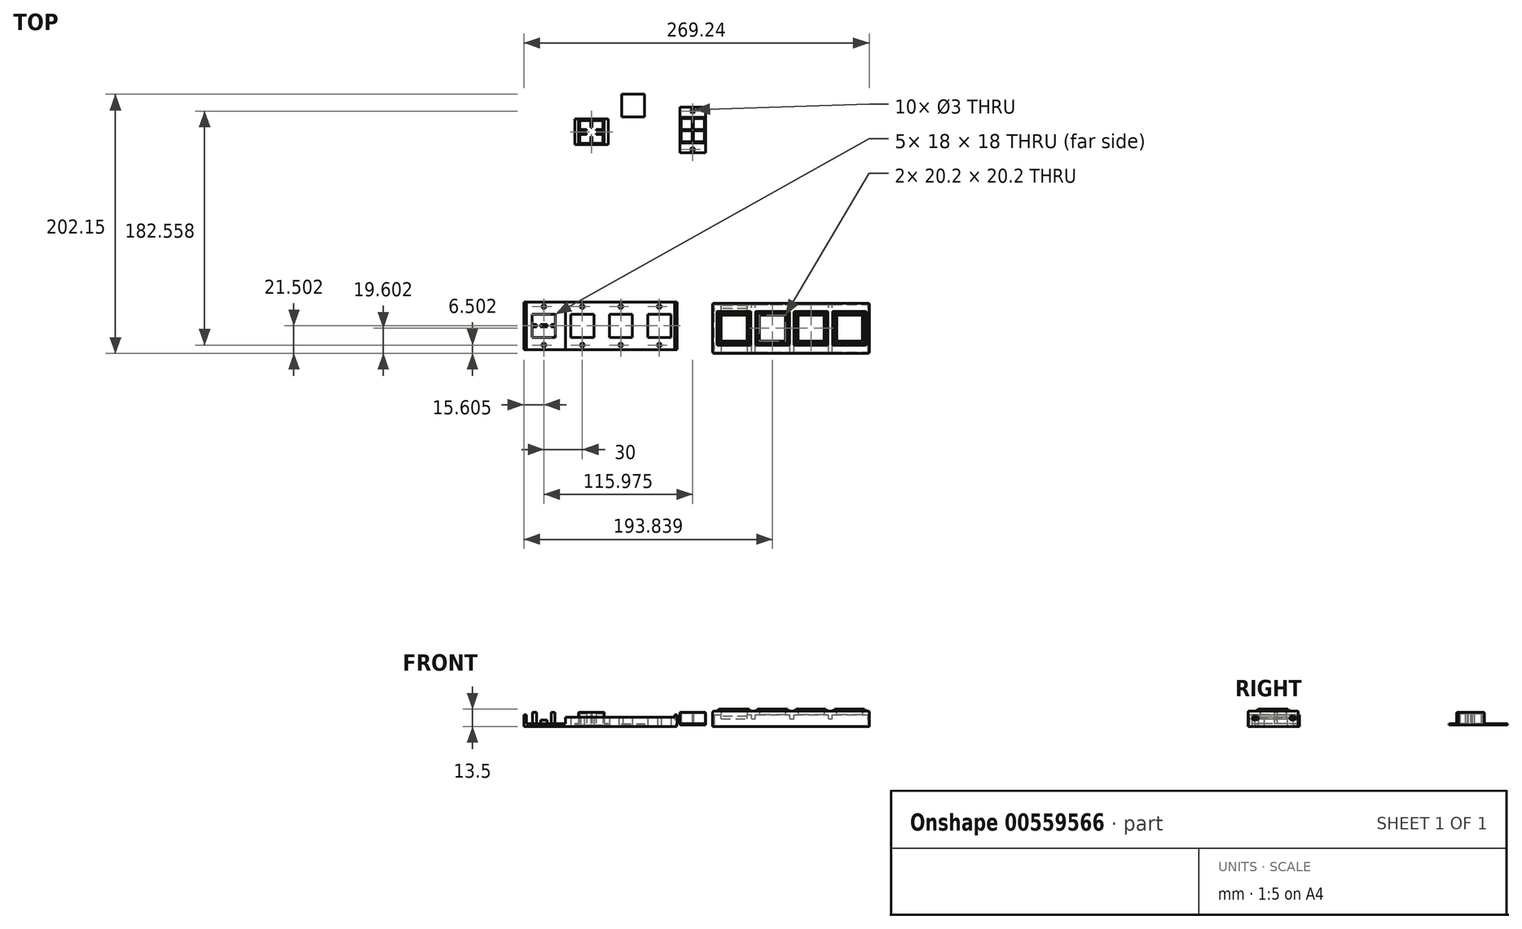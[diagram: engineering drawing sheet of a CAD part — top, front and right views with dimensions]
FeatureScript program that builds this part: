
annotation { "Feature Type Name" : "Feature", "Feature Type Description" : "" }
export const myFeature = defineFeature(function(context is Context, id is Id, definition is map)
    precondition{}
    {
        {
            var Q0;
            Q0=qCreatedBy(makeId("Top.planeOp"),FACE);
            var sketch = newSketch(context, id + "F0", { "sketchPlane" : qUnion([Q0])});
            skPoint(sketch, "E0.middle", {"position": v(0, 0) * mm});
            skLineSegment(sketch, "E1.bottom", {"start": v(10, -10) * mm, "end": v(-10, -10) * mm});
            skLineSegment(sketch, "E1.top", {"start": v(10, 10) * mm, "end": v(-10, 10) * mm});
            skLineSegment(sketch, "E1.left", {"start": v(10, -10) * mm, "end": v(10, 10) * mm});
            skLineSegment(sketch, "E1.right", {"start": v(-10, -10) * mm, "end": v(-10, 10) * mm});
            skSolve(sketch);
        }
        {
            var Q0;
            Q0=makeQuery(id+"F0.imprint","IMPRINT",FACE,{"disambiguationData":[TD([[makeQuery(id+"F0.imprint","IMPRINT",EDGE,{"derivedFrom":sQuery(id+"F0.wireOp",EDGE,"E1.bottom")}),-1.0]])]});
            extrude(context, id + "F1", {"entities" : qUnion([Q0]), "depth" : 10 * mm});
        }
        {
            var Q0;
            Q0=makeQuery(id+"F1.opExtrude","CAP_FACE",FACE,{"disambiguationData":[OSD([sQuery(id+"F0.wireOp",EDGE,"E1.bottom"),sQuery(id+"F0.wireOp",EDGE,"E1.top"),sQuery(id+"F0.wireOp",EDGE,"E1.left"),sQuery(id+"F0.wireOp",EDGE,"E1.right")])],"isStart":true});
            shell(context, id + "F2", {"entities" : qUnion([Q0]), "thickness" : 1 * mm});
        }
        {
            var Q0;
            Q0=qCreatedBy(makeId("Top.planeOp"),FACE);
            var sketch = newSketch(context, id + "F3", { "sketchPlane" : qUnion([Q0])});
            skLineSegment(sketch, "E2.bottom", {"start": v(0.5, -9) * mm, "end": v(-0.5, -9) * mm});
            skLineSegment(sketch, "E2.top", {"start": v(0.5, 9) * mm, "end": v(-0.5, 9) * mm});
            skLineSegment(sketch, "E2.left", {"start": v(0.5, -9) * mm, "end": v(0.5, -0.5) * mm});
            skLineSegment(sketch, "E2.right", {"start": v(-0.5, -9) * mm, "end": v(-0.5, -0.5) * mm});
            skLineSegment(sketch, "E3.bottom", {"start": v(9, 0.5) * mm, "end": v(0.5, 0.5) * mm});
            skLineSegment(sketch, "E3.top", {"start": v(9, -0.5) * mm, "end": v(0.5, -0.5) * mm});
            skLineSegment(sketch, "E3.left", {"start": v(9, 0.5) * mm, "end": v(9, -0.5) * mm});
            skLineSegment(sketch, "E3.right", {"start": v(-9, 0.5) * mm, "end": v(-9, -0.5) * mm});
            skLineSegment(sketch, "E4.trimOffspring", {"start": v(-0.5, 0.5) * mm, "end": v(-0.5, 9) * mm});
            skLineSegment(sketch, "E5.trimOffspring", {"start": v(-0.5, -0.5) * mm, "end": v(-9, -0.5) * mm});
            skLineSegment(sketch, "E6.trimOffspring", {"start": v(0.5, 0.5) * mm, "end": v(0.5, 9) * mm});
            skLineSegment(sketch, "E7.trimOffspring", {"start": v(-0.5, 0.5) * mm, "end": v(-9, 0.5) * mm});
            skSolve(sketch);
        }
        {
            var Q0;
            Q0=qSketchRegion(id+"F3",true);
            extrude(context, id + "F4", {"entities" : qUnion([Q0]), "operationType" : NewBodyOperationType.ADD, "depth" : 9 * mm});
        }
        {
            var Q0;
            Q0=qCreatedBy(makeId("Top.planeOp"),FACE);
            var sketch = newSketch(context, id + "F5", { "sketchPlane" : qUnion([Q0])});
            skLineSegment(sketch, "E8.bottom", {"start": v(-10, -9.5) * mm, "end": v(10, -9.5) * mm});
            skLineSegment(sketch, "E8.top", {"start": v(-10, -17.5) * mm, "end": v(10, -17.5) * mm});
            skLineSegment(sketch, "E8.left", {"start": v(-10, -9.5) * mm, "end": v(-10, -17.5) * mm});
            skLineSegment(sketch, "E8.right", {"start": v(10, -9.5) * mm, "end": v(10, -17.5) * mm});
            skLineSegment(sketch, "E9.bottom", {"start": v(-10, 10) * mm, "end": v(10, 10) * mm});
            skLineSegment(sketch, "E9.top", {"start": v(-10, 18) * mm, "end": v(10, 18) * mm});
            skLineSegment(sketch, "E9.left", {"start": v(-10, 10) * mm, "end": v(-10, 18) * mm});
            skLineSegment(sketch, "E9.right", {"start": v(10, 10) * mm, "end": v(10, 18) * mm});
            skLineSegment(sketch, "E10.bottom", {"start": v(-10, -9.5) * mm, "end": v(-13, -9.5) * mm, "construction": true});
            skLineSegment(sketch, "E10.top", {"start": v(-10, 10) * mm, "end": v(-13, 10) * mm, "construction": true});
            skLineSegment(sketch, "E10.left", {"start": v(-10, -9.5) * mm, "end": v(-10, 10) * mm});
            skLineSegment(sketch, "E10.right", {"start": v(-13, -9.5) * mm, "end": v(-13, 10) * mm, "construction": true});
            skLineSegment(sketch, "E11.bottom", {"start": v(10, -9.5) * mm, "end": v(13, -9.5) * mm, "construction": true});
            skLineSegment(sketch, "E11.top", {"start": v(10, 10) * mm, "end": v(13, 10) * mm, "construction": true});
            skLineSegment(sketch, "E11.left", {"start": v(10, -9.5) * mm, "end": v(10, 10) * mm});
            skLineSegment(sketch, "E11.right", {"start": v(13, -9.5) * mm, "end": v(13, 10) * mm, "construction": true});
            skCircle(sketch, "E12", {"center": v(0, 15) * mm, "radius": 1.5 * mm});
            skCircle(sketch, "E13", {"center": v(0, -15) * mm, "radius": 1.5 * mm});
            skSolve(sketch);
        }
        {
            var Q0;
            Q0=makeQuery(id+"F5.imprint","IMPRINT",FACE,{"disambiguationData":[TD([[makeQuery(id+"F5.imprint","IMPRINT",EDGE,{"derivedFrom":sQuery(id+"F5.wireOp",EDGE,"E10.bottom")}),-1.0]])]});
            var Q1;
            Q1=makeQuery(id+"F5.imprint","IMPRINT",FACE,{"disambiguationData":[TD([[makeQuery(id+"F5.imprint","IMPRINT",EDGE,{"derivedFrom":sQuery(id+"F5.wireOp",EDGE,"E8.bottom")}),-1.0]])]});
            var Q2;
            Q2=makeQuery(id+"F5.imprint","IMPRINT",FACE,{"disambiguationData":[TD([[makeQuery(id+"F5.imprint","IMPRINT",EDGE,{"derivedFrom":sQuery(id+"F5.wireOp",EDGE,"E11.bottom")}),1.0]])]});
            var Q3;
            Q3=makeQuery(id+"F5.imprint","IMPRINT",FACE,{"disambiguationData":[TD([[makeQuery(id+"F5.imprint","IMPRINT",EDGE,{"derivedFrom":sQuery(id+"F5.wireOp",EDGE,"E9.bottom")}),1.0]])]});
            extrude(context, id + "F6", {"entities" : qUnion([Q0, Q1, Q2, Q3]), "operationType" : NewBodyOperationType.ADD, "depth" : 1 * mm});
        }
        {
            var Q0;
            Q0=qCreatedBy(makeId("Top.planeOp"),FACE);
            var sketch = newSketch(context, id + "F7", { "sketchPlane" : qUnion([Q0])});
            skLineSegment(sketch, "E14.bottom", {"start": v(-88.88, 8.7) * mm, "end": v(-68.88, 8.7) * mm});
            skLineSegment(sketch, "E14.top", {"start": v(-88.88, -11.3) * mm, "end": v(-68.88, -11.3) * mm});
            skLineSegment(sketch, "E14.left", {"start": v(-88.88, 8.7) * mm, "end": v(-88.88, -11.3) * mm});
            skLineSegment(sketch, "E14.right", {"start": v(-68.88, 8.7) * mm, "end": v(-68.88, -11.3) * mm});
            skSolve(sketch);
        }
        {
            var Q0;
            Q0=makeQuery(id+"F7.imprint","IMPRINT",FACE,{"disambiguationData":[TD([[makeQuery(id+"F7.imprint","IMPRINT",EDGE,{"derivedFrom":sQuery(id+"F7.wireOp",EDGE,"E14.bottom")}),-1.0]])]});
            extrude(context, id + "F8", {"entities" : qUnion([Q0]), "depth" : 10 * mm});
        }
        {
            var Q0;
            Q0=makeQuery(id+"F13.boolean.opBoolean","MERGE",FACE,{"derivedFrom":[makeQuery(id+"F8.opExtrude","CAP_FACE",FACE,{"disambiguationData":[OSD([sQuery(id+"F7.wireOp",EDGE,"E14.bottom"),sQuery(id+"F7.wireOp",EDGE,"E14.top"),sQuery(id+"F7.wireOp",EDGE,"E14.left"),sQuery(id+"F7.wireOp",EDGE,"E14.right")])],"isStart":true}),makeQuery(id+"F13.opExtrude","CAP_FACE",FACE,{"disambiguationData":[OSD([sQuery(id+"F12.wireOp",EDGE,"E22.bottom"),sQuery(id+"F12.wireOp",EDGE,"E22.top"),sQuery(id+"F12.wireOp",EDGE,"E22.left"),sQuery(id+"F12.wireOp",EDGE,"E22.right"),sQuery(id+"F12.wireOp",EDGE,"E23.trimOffspring"),sQuery(id+"F12.wireOp",EDGE,"E25.trimOffspring"),sQuery(id+"F12.wireOp",EDGE,"E27"),sQuery(id+"F12.wireOp",EDGE,"E28"),sQuery(id+"F12.wireOp",EDGE,"E29.bottom"),sQuery(id+"F12.wireOp",EDGE,"E29.top"),sQuery(id+"F12.wireOp",EDGE,"E29.left"),sQuery(id+"F12.wireOp",EDGE,"E30.bottom"),sQuery(id+"F12.wireOp",EDGE,"E30.top"),sQuery(id+"F12.wireOp",EDGE,"E30.left"),sQuery(id+"F12.wireOp",EDGE,"E31.bottom"),sQuery(id+"F12.wireOp",EDGE,"E31.top"),sQuery(id+"F12.wireOp",EDGE,"E31.right"),sQuery(id+"F12.wireOp",EDGE,"E32.bottom"),sQuery(id+"F12.wireOp",EDGE,"E32.top"),sQuery(id+"F12.wireOp",EDGE,"E32.right")])],"isStart":true})]});
            var sketch = newSketch(context, id + "F9", { "sketchPlane" : qUnion([Q0])});
            skLineSegment(sketch, "E15.bottom", {"start": v(-88.88, 11.3) * mm, "end": v(-68.88, 11.3) * mm});
            skLineSegment(sketch, "E15.top", {"start": v(-88.88, 14.3) * mm, "end": v(-68.88, 14.3) * mm, "construction": true});
            skLineSegment(sketch, "E15.left", {"start": v(-88.88, 11.3) * mm, "end": v(-88.88, 14.3) * mm, "construction": true});
            skLineSegment(sketch, "E15.right", {"start": v(-68.88, 11.3) * mm, "end": v(-68.88, 14.3) * mm, "construction": true});
            skLineSegment(sketch, "E16.bottom", {"start": v(-88.88, -8.7) * mm, "end": v(-68.88, -8.7) * mm});
            skLineSegment(sketch, "E16.top", {"start": v(-88.88, -11.7) * mm, "end": v(-68.88, -11.7) * mm});
            skLineSegment(sketch, "E16.left", {"start": v(-88.88, -8.7) * mm, "end": v(-88.88, -11.7) * mm, "construction": true});
            skLineSegment(sketch, "E16.right", {"start": v(-68.88, -8.7) * mm, "end": v(-68.88, -11.7) * mm, "construction": true});
            skLineSegment(sketch, "E17.bottom", {"start": v(-88.88, -8.7) * mm, "end": v(-91.88, -8.7) * mm});
            skLineSegment(sketch, "E17.top", {"start": v(-88.88, 11.3) * mm, "end": v(-91.88, 11.3) * mm});
            skLineSegment(sketch, "E17.left", {"start": v(-88.88, -8.7) * mm, "end": v(-88.88, 11.3) * mm});
            skLineSegment(sketch, "E17.right", {"start": v(-91.88, -8.7) * mm, "end": v(-91.88, 11.3) * mm});
            skLineSegment(sketch, "E18.bottom", {"start": v(-68.88, -8.7) * mm, "end": v(-65.88, -8.7) * mm});
            skLineSegment(sketch, "E18.top", {"start": v(-68.88, 11.3) * mm, "end": v(-65.88, 11.3) * mm});
            skLineSegment(sketch, "E18.left", {"start": v(-68.88, -8.7) * mm, "end": v(-68.88, 11.3) * mm});
            skLineSegment(sketch, "E18.right", {"start": v(-65.88, -8.7) * mm, "end": v(-65.88, 11.3) * mm});
            skLineSegment(sketch, "E19.bottom", {"start": v(-88.88, -11.7) * mm, "end": v(-68.88, -11.7) * mm, "construction": true});
            skLineSegment(sketch, "E19.top", {"start": v(-88.88, -16.7) * mm, "end": v(-68.88, -16.7) * mm, "construction": true});
            skLineSegment(sketch, "E19.left", {"start": v(-88.88, -11.7) * mm, "end": v(-88.88, -16.7) * mm, "construction": true});
            skLineSegment(sketch, "E19.right", {"start": v(-68.88, -11.7) * mm, "end": v(-68.88, -16.7) * mm, "construction": true});
            skCircle(sketch, "E20", {"center": v(-78.88, -13.7) * mm, "radius": 1.5 * mm, "construction": true});
            skSolve(sketch);
        }
        {
            var Q0;
            Q0=qSketchRegion(id+"F9",true);
            extrude(context, id + "F10", {"entities" : qUnion([Q0]), "operationType" : NewBodyOperationType.ADD, "oppositeDirection" : true, "depth" : 0.95 * mm});
        }
        {
            var Q0;
            Q0=makeQuery(id+"F8.opExtrude","CAP_FACE",FACE,{"disambiguationData":[OSD([sQuery(id+"F7.wireOp",EDGE,"E14.bottom"),sQuery(id+"F7.wireOp",EDGE,"E14.top"),sQuery(id+"F7.wireOp",EDGE,"E14.left"),sQuery(id+"F7.wireOp",EDGE,"E14.right")])],"isStart":true});
            shell(context, id + "F11", {"entities" : qUnion([Q0]), "thickness" : 1 * mm});
        }
        {
            var Q0;
            Q0=qCreatedBy(makeId("Top.planeOp"),FACE);
            var sketch = newSketch(context, id + "F12", { "sketchPlane" : qUnion([Q0])});
            skLineSegment(sketch, "E21.bottom", {"start": v(-87.88, -0.1) * mm, "end": v(-79.38, -0.1) * mm, "construction": true});
            skLineSegment(sketch, "E21.top", {"start": v(-87.88, -2.5) * mm, "end": v(-79.38, -2.5) * mm, "construction": true});
            skLineSegment(sketch, "E21.left", {"start": v(-87.88, -0.1) * mm, "end": v(-87.88, -2.5) * mm, "construction": true});
            skLineSegment(sketch, "E21.right", {"start": v(-69.88, -0.1) * mm, "end": v(-69.88, -2.5) * mm, "construction": true});
            skLineSegment(sketch, "E22.bottom", {"start": v(-79.38, 7.7) * mm, "end": v(-78.38, 7.7) * mm});
            skLineSegment(sketch, "E22.top", {"start": v(-79.38, -10.3) * mm, "end": v(-78.38, -10.3) * mm});
            skLineSegment(sketch, "E22.left", {"start": v(-79.38, 7.7) * mm, "end": v(-79.38, -0.1) * mm});
            skLineSegment(sketch, "E22.right", {"start": v(-78.38, 7.7) * mm, "end": v(-78.38, -0.1) * mm});
            skLineSegment(sketch, "E23.trimOffspring", {"start": v(-79.38, -10.3) * mm, "end": v(-79.38, -2.5) * mm});
            skLineSegment(sketch, "E24.trimOffspring", {"start": v(-78.38, -0.1) * mm, "end": v(-69.88, -0.1) * mm, "construction": true});
            skLineSegment(sketch, "E25.trimOffspring", {"start": v(-78.38, -2.5) * mm, "end": v(-78.38, -10.3) * mm});
            skLineSegment(sketch, "E26.trimOffspring", {"start": v(-78.38, -2.5) * mm, "end": v(-69.88, -2.5) * mm, "construction": true});
            skLineSegment(sketch, "E27", {"start": v(-79.38, -2.5) * mm, "end": v(-79.38, -0.1) * mm});
            skLineSegment(sketch, "E28", {"start": v(-78.38, -2.5) * mm, "end": v(-78.38, -0.1) * mm});
            skLineSegment(sketch, "E29.bottom", {"start": v(-87.88, -2.5) * mm, "end": v(-79.38, -2.5) * mm});
            skLineSegment(sketch, "E29.top", {"start": v(-87.88, -3.3) * mm, "end": v(-79.38, -3.3) * mm});
            skLineSegment(sketch, "E29.left", {"start": v(-87.88, -2.5) * mm, "end": v(-87.88, -3.3) * mm});
            skLineSegment(sketch, "E29.right", {"start": v(-79.38, -2.5) * mm, "end": v(-79.38, -3.3) * mm});
            skLineSegment(sketch, "E30.bottom", {"start": v(-87.88, -0.1) * mm, "end": v(-79.38, -0.1) * mm});
            skLineSegment(sketch, "E30.top", {"start": v(-87.88, 0.7) * mm, "end": v(-79.38, 0.7) * mm});
            skLineSegment(sketch, "E30.left", {"start": v(-87.88, -0.1) * mm, "end": v(-87.88, 0.7) * mm});
            skLineSegment(sketch, "E30.right", {"start": v(-79.38, -0.1) * mm, "end": v(-79.38, 0.7) * mm});
            skLineSegment(sketch, "E31.bottom", {"start": v(-78.38, -3.3) * mm, "end": v(-69.88, -3.3) * mm});
            skLineSegment(sketch, "E31.top", {"start": v(-78.38, -2.5) * mm, "end": v(-69.88, -2.5) * mm});
            skLineSegment(sketch, "E31.left", {"start": v(-78.38, -3.3) * mm, "end": v(-78.38, -2.5) * mm});
            skLineSegment(sketch, "E31.right", {"start": v(-69.88, -3.3) * mm, "end": v(-69.88, -2.5) * mm});
            skLineSegment(sketch, "E32.bottom", {"start": v(-78.38, -0.1) * mm, "end": v(-69.88, -0.1) * mm});
            skLineSegment(sketch, "E32.top", {"start": v(-78.38, 0.7) * mm, "end": v(-69.88, 0.7) * mm});
            skLineSegment(sketch, "E32.left", {"start": v(-78.38, -0.1) * mm, "end": v(-78.38, 0.7) * mm});
            skLineSegment(sketch, "E32.right", {"start": v(-69.88, -0.1) * mm, "end": v(-69.88, 0.7) * mm});
            skSolve(sketch);
        }
        {
            var Q0;
            Q0=makeQuery(id+"F12.imprint","IMPRINT",FACE,{"disambiguationData":[TD([[makeQuery(id+"F12.imprint","IMPRINT",EDGE,{"derivedFrom":sQuery(id+"F12.wireOp",EDGE,"E22.bottom")}),-1.0]])]});
            var Q1;
            Q1=makeQuery(id+"F12.imprint","IMPRINT",FACE,{"disambiguationData":[TD([[makeQuery(id+"F12.imprint","IMPRINT",EDGE,{"derivedFrom":sQuery(id+"F12.wireOp",EDGE,"E29.bottom")}),-1.0]])]});
            var Q2;
            Q2=makeQuery(id+"F12.imprint","IMPRINT",FACE,{"disambiguationData":[TD([[makeQuery(id+"F12.imprint","IMPRINT",EDGE,{"derivedFrom":sQuery(id+"F12.wireOp",EDGE,"E30.bottom")}),1.0]])]});
            var Q3;
            Q3=makeQuery(id+"F12.imprint","IMPRINT",FACE,{"disambiguationData":[TD([[makeQuery(id+"F12.imprint","IMPRINT",EDGE,{"derivedFrom":sQuery(id+"F12.wireOp",EDGE,"E32.bottom")}),1.0]])]});
            var Q4;
            Q4=makeQuery(id+"F12.imprint","IMPRINT",FACE,{"disambiguationData":[TD([[makeQuery(id+"F12.imprint","IMPRINT",EDGE,{"derivedFrom":sQuery(id+"F12.wireOp",EDGE,"E31.bottom")}),1.0]])]});
            var Q5;
            Q5=sQuery(id+"F12.wireOp",EDGE,"E22.left");
            var Q6;
            Q6=sQuery(id+"F12.wireOp",EDGE,"E23.trimOffspring");
            var Q7;
            Q7=sQuery(id+"F12.wireOp",EDGE,"E21.top");
            var Q8;
            Q8=sQuery(id+"F12.wireOp",EDGE,"E24.trimOffspring");
            var Q9;
            Q9=sQuery(id+"F12.wireOp",EDGE,"E22.bottom");
            var Q10;
            Q10=sQuery(id+"F12.wireOp",EDGE,"E22.right");
            var Q11;
            Q11=sQuery(id+"F12.wireOp",EDGE,"E22.top");
            var Q12;
            Q12=sQuery(id+"F12.wireOp",EDGE,"E21.bottom");
            var Q13;
            Q13=sQuery(id+"F12.wireOp",EDGE,"E25.trimOffspring");
            var Q14;
            Q14=sQuery(id+"F12.wireOp",EDGE,"E26.trimOffspring");
            var Q15;
            Q15=sQuery(id+"F12.wireOp",EDGE,"E21.right");
            var Q16;
            Q16=sQuery(id+"F12.wireOp",EDGE,"E21.left");
            extrude(context, id + "F13", {"entities" : qUnion([Q0, Q1, Q2, Q3, Q4]), "operationType" : NewBodyOperationType.ADD, "surfaceEntities" : qUnion([Q5, Q6, Q7, Q8, Q9, Q10, Q11, Q12, Q13, Q14, Q15, Q16]), "depth" : 9 * mm});
        }
        {
            var Q0;
            Q0=makeQuery(id+"F13.boolean.opBoolean","MERGE",FACE,{"derivedFrom":[makeQuery(id+"F8.opExtrude","CAP_FACE",FACE,{"disambiguationData":[OSD([sQuery(id+"F7.wireOp",EDGE,"E14.bottom"),sQuery(id+"F7.wireOp",EDGE,"E14.top"),sQuery(id+"F7.wireOp",EDGE,"E14.left"),sQuery(id+"F7.wireOp",EDGE,"E14.right")])],"isStart":true}),makeQuery(id+"F13.opExtrude","CAP_FACE",FACE,{"disambiguationData":[OSD([sQuery(id+"F12.wireOp",EDGE,"E21.bottom"),sQuery(id+"F12.wireOp",EDGE,"E21.top"),sQuery(id+"F12.wireOp",EDGE,"E21.left"),sQuery(id+"F12.wireOp",EDGE,"E21.right"),sQuery(id+"F12.wireOp",EDGE,"E22.bottom"),sQuery(id+"F12.wireOp",EDGE,"E22.top"),sQuery(id+"F12.wireOp",EDGE,"E22.left"),sQuery(id+"F12.wireOp",EDGE,"E22.right"),sQuery(id+"F12.wireOp",EDGE,"E23.trimOffspring"),sQuery(id+"F12.wireOp",EDGE,"E24.trimOffspring"),sQuery(id+"F12.wireOp",EDGE,"E25.trimOffspring"),sQuery(id+"F12.wireOp",EDGE,"E26.trimOffspring")])],"isStart":true})]});
            var sketch = newSketch(context, id + "F14", { "sketchPlane" : qUnion([Q0])});
            skLineSegment(sketch, "E33.bottom", {"start": v(-75.28, -2.3) * mm, "end": v(-82.48, -2.3) * mm});
            skLineSegment(sketch, "E33.top", {"start": v(-75.28, 4.9) * mm, "end": v(-82.48, 4.9) * mm});
            skLineSegment(sketch, "E33.left", {"start": v(-75.28, -2.3) * mm, "end": v(-75.28, 4.9) * mm});
            skLineSegment(sketch, "E33.right", {"start": v(-82.48, -2.3) * mm, "end": v(-82.48, 4.9) * mm});
            skPoint(sketch, "E33.middle.positionSnap1", {"position": v(-88.88, 1.8) * mm});
            skSolve(sketch);
        }
        {
            var Q0;
            {var subQ1=makeQuery(id+"F13.opExtrude","CAP_EDGE",EDGE,{"disambiguationData":[OSD([sQuery(id+"F12.wireOp",EDGE,"E22.right")])],"isStart":true});var subQ3=sQuery(id+"F14.wireOp",EDGE,"E33.bottom");var subQ4=makeQuery(id+"F14.imprint","INTERSECT",VERTEX,{"derivedFrom":[subQ1,subQ3]});Q0=makeQuery(id+"F14.imprint","IMPRINT",FACE,{"disambiguationData":[TD([[makeQuery(id+"F14.imprint","IMPRINT",EDGE,{"disambiguationData":[TD([[subQ4,-1.0]])],"derivedFrom":subQ3}),-1.0]])]});}
            extrude(context, id + "F15", {"entities" : qUnion([Q0]), "operationType" : NewBodyOperationType.REMOVE, "oppositeDirection" : true, "depth" : 9 * mm});
        }
        {
            var Q0;
            Q0=qCreatedBy(makeId("Top.planeOp"),FACE);
            var sketch = newSketch(context, id + "F16", { "sketchPlane" : qUnion([Q0])});
            skLineSegment(sketch, "E34.bottom", {"start": v(-124.98, -143.56) * mm, "end": v(-106.98, -143.56) * mm});
            skLineSegment(sketch, "E34.top", {"start": v(-124.98, -161.56) * mm, "end": v(-106.98, -161.56) * mm});
            skLineSegment(sketch, "E34.left", {"start": v(-124.98, -143.56) * mm, "end": v(-124.98, -161.56) * mm});
            skLineSegment(sketch, "E34.right", {"start": v(-106.98, -143.56) * mm, "end": v(-106.98, -161.56) * mm});
            skLineSegment(sketch, "E35.bottom", {"start": v(-116.73, -143.56) * mm, "end": v(-115.23, -143.56) * mm, "construction": true});
            skLineSegment(sketch, "E35.top", {"start": v(-116.73, -161.56) * mm, "end": v(-115.23, -161.56) * mm, "construction": true});
            skLineSegment(sketch, "E35.left", {"start": v(-116.73, -143.56) * mm, "end": v(-116.73, -151.56) * mm, "construction": true});
            skLineSegment(sketch, "E35.right", {"start": v(-115.23, -143.56) * mm, "end": v(-115.23, -151.56) * mm, "construction": true});
            skCircle(sketch, "E36", {"center": v(-115.98, -137.56) * mm, "radius": 1.5 * mm});
            skPoint(sketch, "E37", {"position": v(-115.98, -143.56) * mm});
            skCircle(sketch, "E38", {"center": v(-115.98, -167.56) * mm, "radius": 1.5 * mm});
            skLineSegment(sketch, "E39.trimOffspring", {"start": v(-115.23, -151.56) * mm, "end": v(-112.23, -151.56) * mm, "construction": true});
            skLineSegment(sketch, "E40.trimOffspring", {"start": v(-115.23, -153.56) * mm, "end": v(-112.23, -153.56) * mm, "construction": true});
            skLineSegment(sketch, "E41.trimOffspring", {"start": v(-116.73, -153.56) * mm, "end": v(-116.73, -161.56) * mm, "construction": true});
            skLineSegment(sketch, "E42.trimOffspring", {"start": v(-115.23, -153.56) * mm, "end": v(-115.23, -161.56) * mm, "construction": true});
            skLineSegment(sketch, "E43.bottom", {"start": v(-121.73, -143.56) * mm, "end": v(-119.73, -143.56) * mm});
            skLineSegment(sketch, "E43.top", {"start": v(-121.73, -161.56) * mm, "end": v(-119.73, -161.56) * mm});
            skLineSegment(sketch, "E43.left", {"start": v(-121.73, -143.56) * mm, "end": v(-121.73, -151.56) * mm});
            skLineSegment(sketch, "E43.right", {"start": v(-119.73, -143.56) * mm, "end": v(-119.73, -151.56) * mm});
            skLineSegment(sketch, "E44.bottom", {"start": v(-112.23, -143.56) * mm, "end": v(-110.23, -143.56) * mm});
            skLineSegment(sketch, "E44.top", {"start": v(-112.23, -161.56) * mm, "end": v(-110.23, -161.56) * mm});
            skLineSegment(sketch, "E44.left", {"start": v(-112.23, -143.56) * mm, "end": v(-112.23, -151.56) * mm});
            skLineSegment(sketch, "E44.right", {"start": v(-110.23, -143.56) * mm, "end": v(-110.23, -151.56) * mm});
            skLineSegment(sketch, "E45.bottom", {"start": v(-124.98, -151.56) * mm, "end": v(-121.73, -151.56) * mm});
            skLineSegment(sketch, "E45.top", {"start": v(-124.98, -153.56) * mm, "end": v(-121.73, -153.56) * mm});
            skLineSegment(sketch, "E45.left", {"start": v(-124.98, -151.56) * mm, "end": v(-124.98, -153.56) * mm});
            skLineSegment(sketch, "E45.right", {"start": v(-106.98, -151.56) * mm, "end": v(-106.98, -153.56) * mm});
            skLineSegment(sketch, "E46.trimOffspring", {"start": v(-121.73, -153.56) * mm, "end": v(-121.73, -161.56) * mm});
            skLineSegment(sketch, "E47.trimOffspring", {"start": v(-119.73, -153.56) * mm, "end": v(-119.73, -161.56) * mm});
            skLineSegment(sketch, "E48.trimOffspring", {"start": v(-119.73, -151.56) * mm, "end": v(-116.73, -151.56) * mm, "construction": true});
            skLineSegment(sketch, "E49.trimOffspring", {"start": v(-119.73, -153.56) * mm, "end": v(-116.73, -153.56) * mm, "construction": true});
            skLineSegment(sketch, "E50.trimOffspring", {"start": v(-119.73, -151.56) * mm, "end": v(-112.23, -151.56) * mm});
            skLineSegment(sketch, "E51.trimOffspring", {"start": v(-119.73, -153.56) * mm, "end": v(-112.23, -153.56) * mm});
            skLineSegment(sketch, "E52.trimOffspring", {"start": v(-112.23, -153.56) * mm, "end": v(-112.23, -161.56) * mm});
            skLineSegment(sketch, "E53.trimOffspring", {"start": v(-110.23, -153.56) * mm, "end": v(-110.23, -161.56) * mm});
            skLineSegment(sketch, "E54.trimOffspring", {"start": v(-110.23, -151.56) * mm, "end": v(-106.98, -151.56) * mm});
            skLineSegment(sketch, "E55.trimOffspring", {"start": v(-110.23, -153.56) * mm, "end": v(-106.98, -153.56) * mm});
            skLineSegment(sketch, "E56.bottom", {"start": v(-94.98, -143.56) * mm, "end": v(-76.98, -143.56) * mm});
            skLineSegment(sketch, "E56.top", {"start": v(-94.98, -161.56) * mm, "end": v(-76.98, -161.56) * mm});
            skLineSegment(sketch, "E56.left", {"start": v(-94.98, -143.56) * mm, "end": v(-94.98, -161.56) * mm});
            skLineSegment(sketch, "E56.right", {"start": v(-76.98, -143.56) * mm, "end": v(-76.98, -161.56) * mm});
            skLineSegment(sketch, "E57.bottom", {"start": v(-86.73, -143.56) * mm, "end": v(-85.23, -143.56) * mm, "construction": true});
            skLineSegment(sketch, "E57.top", {"start": v(-86.73, -161.56) * mm, "end": v(-85.23, -161.56) * mm, "construction": true});
            skLineSegment(sketch, "E57.left", {"start": v(-86.73, -143.56) * mm, "end": v(-86.73, -151.56) * mm, "construction": true});
            skLineSegment(sketch, "E57.right", {"start": v(-85.23, -143.56) * mm, "end": v(-85.23, -151.56) * mm, "construction": true});
            skLineSegment(sketch, "E58.bottom", {"start": v(-94.98, -151.56) * mm, "end": v(-91.73, -151.56) * mm, "construction": true});
            skLineSegment(sketch, "E58.top", {"start": v(-94.98, -153.56) * mm, "end": v(-91.73, -153.56) * mm, "construction": true});
            skLineSegment(sketch, "E58.left", {"start": v(-94.98, -151.56) * mm, "end": v(-94.98, -153.56) * mm, "construction": true});
            skLineSegment(sketch, "E58.right", {"start": v(-76.98, -151.56) * mm, "end": v(-76.98, -153.56) * mm, "construction": true});
            skCircle(sketch, "E59", {"center": v(-85.98, -137.56) * mm, "radius": 1.5 * mm});
            skPoint(sketch, "E60", {"position": v(-85.98, -143.56) * mm});
            skCircle(sketch, "E61", {"center": v(-85.98, -167.56) * mm, "radius": 1.5 * mm});
            skLineSegment(sketch, "E62.trimOffspring", {"start": v(-85.23, -151.56) * mm, "end": v(-82.23, -151.56) * mm, "construction": true});
            skLineSegment(sketch, "E63.trimOffspring", {"start": v(-85.23, -153.56) * mm, "end": v(-82.23, -153.56) * mm, "construction": true});
            skLineSegment(sketch, "E64.trimOffspring", {"start": v(-86.73, -153.56) * mm, "end": v(-86.73, -161.56) * mm, "construction": true});
            skLineSegment(sketch, "E65.trimOffspring", {"start": v(-85.23, -153.56) * mm, "end": v(-85.23, -161.56) * mm, "construction": true});
            skLineSegment(sketch, "E66.bottom", {"start": v(-91.73, -143.56) * mm, "end": v(-89.73, -143.56) * mm});
            skLineSegment(sketch, "E66.top", {"start": v(-91.73, -161.56) * mm, "end": v(-89.73, -161.56) * mm});
            skLineSegment(sketch, "E66.left", {"start": v(-91.73, -143.56) * mm, "end": v(-91.73, -151.56) * mm});
            skLineSegment(sketch, "E66.right", {"start": v(-89.73, -143.56) * mm, "end": v(-89.73, -151.56) * mm});
            skLineSegment(sketch, "E67.bottom", {"start": v(-82.23, -143.56) * mm, "end": v(-80.23, -143.56) * mm});
            skLineSegment(sketch, "E67.top", {"start": v(-82.23, -161.56) * mm, "end": v(-80.23, -161.56) * mm});
            skLineSegment(sketch, "E67.left", {"start": v(-82.23, -143.56) * mm, "end": v(-82.23, -151.56) * mm});
            skLineSegment(sketch, "E67.right", {"start": v(-80.23, -143.56) * mm, "end": v(-80.23, -151.56) * mm});
            skLineSegment(sketch, "E68.bottom", {"start": v(-94.98, -151.56) * mm, "end": v(-91.73, -151.56) * mm});
            skLineSegment(sketch, "E68.top", {"start": v(-94.98, -153.56) * mm, "end": v(-91.73, -153.56) * mm});
            skLineSegment(sketch, "E68.left", {"start": v(-94.98, -151.56) * mm, "end": v(-94.98, -153.56) * mm});
            skLineSegment(sketch, "E68.right", {"start": v(-76.98, -151.56) * mm, "end": v(-76.98, -153.56) * mm});
            skLineSegment(sketch, "E69.trimOffspring", {"start": v(-91.73, -153.56) * mm, "end": v(-91.73, -161.56) * mm});
            skLineSegment(sketch, "E70.trimOffspring", {"start": v(-89.73, -153.56) * mm, "end": v(-89.73, -161.56) * mm});
            skLineSegment(sketch, "E71.trimOffspring", {"start": v(-89.73, -151.56) * mm, "end": v(-86.73, -151.56) * mm, "construction": true});
            skLineSegment(sketch, "E72.trimOffspring", {"start": v(-89.73, -153.56) * mm, "end": v(-86.73, -153.56) * mm, "construction": true});
            skLineSegment(sketch, "E73.trimOffspring", {"start": v(-89.73, -151.56) * mm, "end": v(-82.23, -151.56) * mm});
            skLineSegment(sketch, "E74.trimOffspring", {"start": v(-89.73, -153.56) * mm, "end": v(-82.23, -153.56) * mm});
            skLineSegment(sketch, "E75.trimOffspring", {"start": v(-82.23, -153.56) * mm, "end": v(-82.23, -161.56) * mm});
            skLineSegment(sketch, "E76.trimOffspring", {"start": v(-80.23, -151.56) * mm, "end": v(-76.98, -151.56) * mm, "construction": true});
            skLineSegment(sketch, "E77.trimOffspring", {"start": v(-80.23, -153.56) * mm, "end": v(-80.23, -161.56) * mm});
            skLineSegment(sketch, "E78.trimOffspring", {"start": v(-80.23, -151.56) * mm, "end": v(-76.98, -151.56) * mm});
            skLineSegment(sketch, "E79.trimOffspring", {"start": v(-80.23, -153.56) * mm, "end": v(-76.98, -153.56) * mm, "construction": true});
            skLineSegment(sketch, "E80.trimOffspring", {"start": v(-80.23, -153.56) * mm, "end": v(-76.98, -153.56) * mm});
            skLineSegment(sketch, "E81.bottom", {"start": v(-64.98, -143.56) * mm, "end": v(-46.98, -143.56) * mm});
            skLineSegment(sketch, "E81.top", {"start": v(-64.98, -161.56) * mm, "end": v(-46.98, -161.56) * mm});
            skLineSegment(sketch, "E81.left", {"start": v(-64.98, -143.56) * mm, "end": v(-64.98, -161.56) * mm});
            skLineSegment(sketch, "E81.right", {"start": v(-46.98, -143.56) * mm, "end": v(-46.98, -161.56) * mm});
            skLineSegment(sketch, "E82.bottom", {"start": v(-64.98, -161.56) * mm, "end": v(-47.98, -161.56) * mm});
            skLineSegment(sketch, "E83.bottom", {"start": v(-56.73, -143.56) * mm, "end": v(-55.23, -143.56) * mm, "construction": true});
            skLineSegment(sketch, "E83.top", {"start": v(-56.73, -161.56) * mm, "end": v(-55.23, -161.56) * mm, "construction": true});
            skLineSegment(sketch, "E83.left", {"start": v(-56.73, -143.56) * mm, "end": v(-56.73, -151.56) * mm, "construction": true});
            skLineSegment(sketch, "E83.right", {"start": v(-55.23, -143.56) * mm, "end": v(-55.23, -151.56) * mm, "construction": true});
            skLineSegment(sketch, "E84.bottom", {"start": v(-64.98, -151.56) * mm, "end": v(-61.73, -151.56) * mm, "construction": true});
            skLineSegment(sketch, "E84.top", {"start": v(-64.98, -153.56) * mm, "end": v(-61.73, -153.56) * mm, "construction": true});
            skLineSegment(sketch, "E84.left", {"start": v(-64.98, -151.56) * mm, "end": v(-64.98, -153.56) * mm, "construction": true});
            skLineSegment(sketch, "E84.right", {"start": v(-46.98, -151.56) * mm, "end": v(-46.98, -153.56) * mm, "construction": true});
            skCircle(sketch, "E85", {"center": v(-55.98, -137.56) * mm, "radius": 1.5 * mm});
            skPoint(sketch, "E86", {"position": v(-55.98, -143.56) * mm});
            skCircle(sketch, "E87", {"center": v(-55.98, -167.56) * mm, "radius": 1.5 * mm});
            skLineSegment(sketch, "E88.trimOffspring", {"start": v(-55.23, -151.56) * mm, "end": v(-52.23, -151.56) * mm, "construction": true});
            skLineSegment(sketch, "E89.trimOffspring", {"start": v(-55.23, -153.56) * mm, "end": v(-52.23, -153.56) * mm, "construction": true});
            skLineSegment(sketch, "E90.trimOffspring", {"start": v(-56.73, -153.56) * mm, "end": v(-56.73, -161.56) * mm, "construction": true});
            skLineSegment(sketch, "E91.trimOffspring", {"start": v(-55.23, -153.56) * mm, "end": v(-55.23, -161.56) * mm, "construction": true});
            skLineSegment(sketch, "E92.bottom", {"start": v(-61.73, -143.56) * mm, "end": v(-59.73, -143.56) * mm});
            skLineSegment(sketch, "E92.top", {"start": v(-61.73, -161.56) * mm, "end": v(-59.73, -161.56) * mm});
            skLineSegment(sketch, "E92.left", {"start": v(-61.73, -143.56) * mm, "end": v(-61.73, -151.56) * mm});
            skLineSegment(sketch, "E92.right", {"start": v(-59.73, -143.56) * mm, "end": v(-59.73, -151.56) * mm});
            skLineSegment(sketch, "E93.bottom", {"start": v(-52.23, -143.56) * mm, "end": v(-50.23, -143.56) * mm});
            skLineSegment(sketch, "E93.top", {"start": v(-52.23, -161.56) * mm, "end": v(-50.23, -161.56) * mm});
            skLineSegment(sketch, "E93.left", {"start": v(-52.23, -143.56) * mm, "end": v(-52.23, -151.56) * mm});
            skLineSegment(sketch, "E93.right", {"start": v(-50.23, -143.56) * mm, "end": v(-50.23, -151.56) * mm});
            skLineSegment(sketch, "E94.bottom", {"start": v(-64.98, -151.56) * mm, "end": v(-61.73, -151.56) * mm});
            skLineSegment(sketch, "E94.top", {"start": v(-64.98, -153.56) * mm, "end": v(-61.73, -153.56) * mm});
            skLineSegment(sketch, "E94.left", {"start": v(-64.98, -151.56) * mm, "end": v(-64.98, -153.56) * mm});
            skLineSegment(sketch, "E94.right", {"start": v(-46.98, -151.56) * mm, "end": v(-46.98, -153.56) * mm});
            skLineSegment(sketch, "E95.trimOffspring", {"start": v(-61.73, -153.56) * mm, "end": v(-61.73, -161.56) * mm});
            skLineSegment(sketch, "E96.trimOffspring", {"start": v(-59.73, -153.56) * mm, "end": v(-59.73, -161.56) * mm});
            skLineSegment(sketch, "E97.trimOffspring", {"start": v(-59.73, -151.56) * mm, "end": v(-56.73, -151.56) * mm, "construction": true});
            skLineSegment(sketch, "E98.trimOffspring", {"start": v(-59.73, -153.56) * mm, "end": v(-56.73, -153.56) * mm, "construction": true});
            skLineSegment(sketch, "E99.trimOffspring", {"start": v(-59.73, -151.56) * mm, "end": v(-52.23, -151.56) * mm});
            skLineSegment(sketch, "E100.trimOffspring", {"start": v(-59.73, -153.56) * mm, "end": v(-52.23, -153.56) * mm});
            skLineSegment(sketch, "E101.trimOffspring", {"start": v(-52.23, -153.56) * mm, "end": v(-52.23, -161.56) * mm});
            skLineSegment(sketch, "E102.trimOffspring", {"start": v(-50.23, -151.56) * mm, "end": v(-46.98, -151.56) * mm, "construction": true});
            skLineSegment(sketch, "E103.trimOffspring", {"start": v(-50.23, -153.56) * mm, "end": v(-50.23, -161.56) * mm});
            skLineSegment(sketch, "E104.trimOffspring", {"start": v(-50.23, -151.56) * mm, "end": v(-46.98, -151.56) * mm});
            skLineSegment(sketch, "E105.trimOffspring", {"start": v(-50.23, -153.56) * mm, "end": v(-46.98, -153.56) * mm, "construction": true});
            skLineSegment(sketch, "E106.trimOffspring", {"start": v(-50.23, -153.56) * mm, "end": v(-46.98, -153.56) * mm});
            skLineSegment(sketch, "E107.bottom", {"start": v(-34.98, -143.56) * mm, "end": v(-16.98, -143.56) * mm});
            skLineSegment(sketch, "E107.top", {"start": v(-34.98, -161.56) * mm, "end": v(-16.98, -161.56) * mm});
            skLineSegment(sketch, "E107.left", {"start": v(-34.98, -143.56) * mm, "end": v(-34.98, -161.56) * mm});
            skLineSegment(sketch, "E107.right", {"start": v(-16.98, -143.56) * mm, "end": v(-16.98, -161.56) * mm});
            skLineSegment(sketch, "E108.bottom", {"start": v(-34.98, -161.56) * mm, "end": v(-17.98, -161.56) * mm});
            skLineSegment(sketch, "E109.bottom", {"start": v(-26.73, -143.56) * mm, "end": v(-25.23, -143.56) * mm, "construction": true});
            skLineSegment(sketch, "E109.top", {"start": v(-26.73, -161.56) * mm, "end": v(-25.23, -161.56) * mm, "construction": true});
            skLineSegment(sketch, "E109.left", {"start": v(-26.73, -143.56) * mm, "end": v(-26.73, -151.56) * mm, "construction": true});
            skLineSegment(sketch, "E109.right", {"start": v(-25.23, -143.56) * mm, "end": v(-25.23, -151.56) * mm, "construction": true});
            skLineSegment(sketch, "E110.bottom", {"start": v(-34.98, -151.56) * mm, "end": v(-31.73, -151.56) * mm, "construction": true});
            skLineSegment(sketch, "E110.top", {"start": v(-34.98, -153.56) * mm, "end": v(-31.73, -153.56) * mm, "construction": true});
            skLineSegment(sketch, "E110.left", {"start": v(-34.98, -151.56) * mm, "end": v(-34.98, -153.56) * mm, "construction": true});
            skLineSegment(sketch, "E110.right", {"start": v(-16.98, -151.56) * mm, "end": v(-16.98, -153.56) * mm, "construction": true});
            skCircle(sketch, "E111", {"center": v(-25.98, -137.56) * mm, "radius": 1.5 * mm});
            skPoint(sketch, "E112", {"position": v(-25.98, -143.56) * mm});
            skCircle(sketch, "E113", {"center": v(-25.98, -167.56) * mm, "radius": 1.5 * mm});
            skLineSegment(sketch, "E114.trimOffspring", {"start": v(-25.23, -151.56) * mm, "end": v(-22.23, -151.56) * mm, "construction": true});
            skLineSegment(sketch, "E115.trimOffspring", {"start": v(-25.23, -153.56) * mm, "end": v(-22.23, -153.56) * mm, "construction": true});
            skLineSegment(sketch, "E116.trimOffspring", {"start": v(-26.73, -153.56) * mm, "end": v(-26.73, -161.56) * mm, "construction": true});
            skLineSegment(sketch, "E117.trimOffspring", {"start": v(-25.23, -153.56) * mm, "end": v(-25.23, -161.56) * mm, "construction": true});
            skLineSegment(sketch, "E118.bottom", {"start": v(-31.73, -143.56) * mm, "end": v(-29.73, -143.56) * mm});
            skLineSegment(sketch, "E118.top", {"start": v(-31.73, -161.56) * mm, "end": v(-29.73, -161.56) * mm});
            skLineSegment(sketch, "E118.left", {"start": v(-31.73, -143.56) * mm, "end": v(-31.73, -151.56) * mm});
            skLineSegment(sketch, "E118.right", {"start": v(-29.73, -143.56) * mm, "end": v(-29.73, -151.56) * mm});
            skLineSegment(sketch, "E119.bottom", {"start": v(-22.23, -143.56) * mm, "end": v(-20.23, -143.56) * mm});
            skLineSegment(sketch, "E119.top", {"start": v(-22.23, -161.56) * mm, "end": v(-20.23, -161.56) * mm});
            skLineSegment(sketch, "E119.left", {"start": v(-22.23, -143.56) * mm, "end": v(-22.23, -151.56) * mm});
            skLineSegment(sketch, "E119.right", {"start": v(-20.23, -143.56) * mm, "end": v(-20.23, -151.56) * mm});
            skLineSegment(sketch, "E120.bottom", {"start": v(-34.98, -151.56) * mm, "end": v(-31.73, -151.56) * mm});
            skLineSegment(sketch, "E120.top", {"start": v(-34.98, -153.56) * mm, "end": v(-31.73, -153.56) * mm});
            skLineSegment(sketch, "E120.left", {"start": v(-34.98, -151.56) * mm, "end": v(-34.98, -153.56) * mm});
            skLineSegment(sketch, "E120.right", {"start": v(-16.98, -151.56) * mm, "end": v(-16.98, -153.56) * mm});
            skLineSegment(sketch, "E121.trimOffspring", {"start": v(-31.73, -153.56) * mm, "end": v(-31.73, -161.56) * mm});
            skLineSegment(sketch, "E122.trimOffspring", {"start": v(-29.73, -153.56) * mm, "end": v(-29.73, -161.56) * mm});
            skLineSegment(sketch, "E123.trimOffspring", {"start": v(-29.73, -151.56) * mm, "end": v(-26.73, -151.56) * mm, "construction": true});
            skLineSegment(sketch, "E124.trimOffspring", {"start": v(-29.73, -153.56) * mm, "end": v(-26.73, -153.56) * mm, "construction": true});
            skLineSegment(sketch, "E125.trimOffspring", {"start": v(-29.73, -151.56) * mm, "end": v(-22.23, -151.56) * mm});
            skLineSegment(sketch, "E126.trimOffspring", {"start": v(-29.73, -153.56) * mm, "end": v(-22.23, -153.56) * mm});
            skLineSegment(sketch, "E127.trimOffspring", {"start": v(-22.23, -153.56) * mm, "end": v(-22.23, -161.56) * mm});
            skLineSegment(sketch, "E128.trimOffspring", {"start": v(-20.23, -151.56) * mm, "end": v(-16.98, -151.56) * mm, "construction": true});
            skLineSegment(sketch, "E129.trimOffspring", {"start": v(-20.23, -153.56) * mm, "end": v(-20.23, -161.56) * mm});
            skLineSegment(sketch, "E130.trimOffspring", {"start": v(-20.23, -151.56) * mm, "end": v(-16.98, -151.56) * mm});
            skLineSegment(sketch, "E131.trimOffspring", {"start": v(-20.23, -153.56) * mm, "end": v(-16.98, -153.56) * mm, "construction": true});
            skLineSegment(sketch, "E132.trimOffspring", {"start": v(-20.23, -153.56) * mm, "end": v(-16.98, -153.56) * mm});
            skLineSegment(sketch, "E133.bottom", {"start": v(-129.58, -134.06) * mm, "end": v(-12.58, -134.06) * mm});
            skLineSegment(sketch, "E133.top", {"start": v(-129.58, -171.06) * mm, "end": v(-12.58, -171.06) * mm});
            skLineSegment(sketch, "E133.left", {"start": v(-129.58, -134.06) * mm, "end": v(-129.58, -171.06) * mm});
            skLineSegment(sketch, "E133.right", {"start": v(-12.58, -134.06) * mm, "end": v(-12.58, -171.06) * mm});
            skSolve(sketch);
        }
        {
            var Q0;
            Q0=makeQuery(id+"F16.imprint","IMPRINT",FACE,{"disambiguationData":[TD([[makeQuery(id+"F16.imprint","IMPRINT",EDGE,{"derivedFrom":sQuery(id+"F16.wireOp",EDGE,"E36")}),-1.0]])]});
            var Q1;
            Q1=makeQuery(id+"F16.imprint","IMPRINT",FACE,{"disambiguationData":[TD([[makeQuery(id+"F16.imprint","IMPRINT",EDGE,{"derivedFrom":sQuery(id+"F16.wireOp",EDGE,"E43.bottom")}),-1.0]])]});
            var Q2;
            Q2=makeQuery(id+"F16.imprint","IMPRINT",FACE,{"disambiguationData":[TD([[makeQuery(id+"F16.imprint","IMPRINT",EDGE,{"derivedFrom":sQuery(id+"F16.wireOp",EDGE,"E66.bottom")}),-1.0]])]});
            var Q3;
            Q3=makeQuery(id+"F16.imprint","IMPRINT",FACE,{"disambiguationData":[TD([[makeQuery(id+"F16.imprint","IMPRINT",EDGE,{"derivedFrom":sQuery(id+"F16.wireOp",EDGE,"E92.bottom")}),-1.0]])]});
            var Q4;
            Q4=makeQuery(id+"F16.imprint","IMPRINT",FACE,{"disambiguationData":[TD([[makeQuery(id+"F16.imprint","IMPRINT",EDGE,{"derivedFrom":sQuery(id+"F16.wireOp",EDGE,"E118.bottom")}),-1.0]])]});
            extrude(context, id + "F17", {"entities" : qUnion([Q0, Q1, Q2, Q3, Q4]), "depth" : 1 * mm});
        }
        {
            var Q0;
            Q0=qCreatedBy(makeId("Top.planeOp"),FACE);
            var sketch = newSketch(context, id + "F18", { "sketchPlane" : qUnion([Q0])});
            skLineSegment(sketch, "E134.bottom", {"start": v(15.66, -134.86) * mm, "end": v(137.66, -134.86) * mm});
            skLineSegment(sketch, "E134.top", {"start": v(15.66, -174.06) * mm, "end": v(137.66, -174.06) * mm});
            skLineSegment(sketch, "E134.left", {"start": v(15.66, -134.86) * mm, "end": v(15.66, -174.06) * mm});
            skLineSegment(sketch, "E134.right", {"start": v(137.66, -134.86) * mm, "end": v(137.66, -174.06) * mm});
            skLineSegment(sketch, "E135.bottom", {"start": v(22.06, -144.26) * mm, "end": v(42.46, -144.26) * mm});
            skLineSegment(sketch, "E135.top", {"start": v(22.06, -164.66) * mm, "end": v(42.46, -164.66) * mm});
            skLineSegment(sketch, "E135.left", {"start": v(22.06, -144.26) * mm, "end": v(22.06, -164.66) * mm});
            skLineSegment(sketch, "E135.right", {"start": v(42.46, -144.26) * mm, "end": v(42.46, -164.66) * mm});
            skCircle(sketch, "E136", {"center": v(31.96, -139.46) * mm, "radius": 1.5 * mm, "construction": true});
            skCircle(sketch, "E137", {"center": v(31.96, -169.46) * mm, "radius": 1.5 * mm, "construction": true});
            skLineSegment(sketch, "E138.bottom", {"start": v(52.16, -144.36) * mm, "end": v(72.36, -144.36) * mm});
            skLineSegment(sketch, "E138.top", {"start": v(52.16, -164.56) * mm, "end": v(72.36, -164.56) * mm});
            skLineSegment(sketch, "E138.left", {"start": v(52.16, -144.36) * mm, "end": v(52.16, -164.56) * mm});
            skLineSegment(sketch, "E138.right", {"start": v(72.36, -144.36) * mm, "end": v(72.36, -164.56) * mm});
            skCircle(sketch, "E139", {"center": v(62.26, -139.46) * mm, "radius": 1.5 * mm, "construction": true});
            skCircle(sketch, "E140", {"center": v(62.26, -169.46) * mm, "radius": 1.5 * mm, "construction": true});
            skLineSegment(sketch, "E141.bottom", {"start": v(82.16, -144.36) * mm, "end": v(102.36, -144.36) * mm});
            skLineSegment(sketch, "E141.top", {"start": v(82.16, -164.56) * mm, "end": v(102.36, -164.56) * mm});
            skLineSegment(sketch, "E141.left", {"start": v(82.16, -144.36) * mm, "end": v(82.16, -164.56) * mm});
            skLineSegment(sketch, "E141.right", {"start": v(102.36, -144.36) * mm, "end": v(102.36, -164.56) * mm});
            skCircle(sketch, "E142", {"center": v(92.26, -139.46) * mm, "radius": 1.5 * mm, "construction": true});
            skCircle(sketch, "E143", {"center": v(92.26, -169.46) * mm, "radius": 1.5 * mm, "construction": true});
            skPoint(sketch, "E143.centerSnap0", {"position": v(92.26, -164.56) * mm});
            skLineSegment(sketch, "E144.bottom", {"start": v(112.16, -144.36) * mm, "end": v(132.36, -144.36) * mm});
            skLineSegment(sketch, "E144.top", {"start": v(112.16, -164.56) * mm, "end": v(132.36, -164.56) * mm});
            skLineSegment(sketch, "E144.left", {"start": v(112.16, -144.36) * mm, "end": v(112.16, -164.56) * mm});
            skLineSegment(sketch, "E144.right", {"start": v(132.36, -144.36) * mm, "end": v(132.36, -164.56) * mm});
            skCircle(sketch, "E145", {"center": v(122.26, -139.46) * mm, "radius": 1.5 * mm, "construction": true});
            skCircle(sketch, "E146", {"center": v(122.26, -169.46) * mm, "radius": 1.5 * mm, "construction": true});
            skLineSegment(sketch, "E147.bottom", {"start": v(23.26, -145.46) * mm, "end": v(41.26, -145.46) * mm, "construction": true});
            skLineSegment(sketch, "E147.top", {"start": v(23.26, -163.46) * mm, "end": v(41.26, -163.46) * mm, "construction": true});
            skLineSegment(sketch, "E147.left", {"start": v(23.26, -145.46) * mm, "end": v(23.26, -163.46) * mm, "construction": true});
            skLineSegment(sketch, "E147.right", {"start": v(41.26, -145.46) * mm, "end": v(41.26, -163.46) * mm, "construction": true});
            skSolve(sketch);
        }
        {
            var Q0;
            Q0=qSketchRegion(id+"F18",true);
            extrude(context, id + "F19", {"entities" : qUnion([Q0]), "depth" : 11 * mm});
        }
        {
            var Q0;
            Q0=makeQuery(id+"F19.opExtrude","CAP_FACE",FACE,{"disambiguationData":[OSD([sQuery(id+"F18.wireOp",EDGE,"E134.bottom"),sQuery(id+"F18.wireOp",EDGE,"E134.top"),sQuery(id+"F18.wireOp",EDGE,"E134.left"),sQuery(id+"F18.wireOp",EDGE,"E134.right")])],"isStart":true});
            var sketch = newSketch(context, id + "F20", { "sketchPlane" : qUnion([Q0])});
            skLineSegment(sketch, "E148.bottom", {"start": v(16.66, 173.06) * mm, "end": v(136.66, 173.06) * mm});
            skLineSegment(sketch, "E148.top", {"start": v(16.66, 135.86) * mm, "end": v(136.66, 135.86) * mm});
            skLineSegment(sketch, "E148.left", {"start": v(16.66, 173.06) * mm, "end": v(16.66, 135.86) * mm});
            skLineSegment(sketch, "E148.right", {"start": v(136.66, 173.06) * mm, "end": v(136.66, 135.86) * mm});
            skSolve(sketch);
        }
        {
            var Q0;
            Q0=qSketchRegion(id+"F20",true);
            extrude(context, id + "F21", {"entities" : qUnion([Q0]), "operationType" : NewBodyOperationType.REMOVE, "oppositeDirection" : true, "depth" : 8 * mm});
        }
        {
            var Q0;
            Q0=makeQuery(id+"F17.opExtrude","CAP_FACE",FACE,{"disambiguationData":[OSD([sQuery(id+"F16.wireOp",EDGE,"55227c07-3752-4080-a22d-609154aa437d.0"),sQuery(id+"F16.wireOp",EDGE,"55227c07-3752-4080-a22d-609154aa437d.1"),sQuery(id+"F16.wireOp",EDGE,"55227c07-3752-4080-a22d-609154aa437d.2"),sQuery(id+"F16.wireOp",EDGE,"55227c07-3752-4080-a22d-609154aa437d.3"),sQuery(id+"F16.wireOp",EDGE,"E36"),sQuery(id+"F16.wireOp",EDGE,"E38"),sQuery(id+"F16.wireOp",EDGE,"E43.left"),sQuery(id+"F16.wireOp",EDGE,"E43.right"),sQuery(id+"F16.wireOp",EDGE,"E44.left"),sQuery(id+"F16.wireOp",EDGE,"E44.right"),sQuery(id+"F16.wireOp",EDGE,"E45.bottom"),sQuery(id+"F16.wireOp",EDGE,"E45.top"),sQuery(id+"F16.wireOp",EDGE,"E46.trimOffspring"),sQuery(id+"F16.wireOp",EDGE,"E47.trimOffspring"),sQuery(id+"F16.wireOp",EDGE,"E50.trimOffspring"),sQuery(id+"F16.wireOp",EDGE,"E51.trimOffspring"),sQuery(id+"F16.wireOp",EDGE,"E52.trimOffspring"),sQuery(id+"F16.wireOp",EDGE,"E53.trimOffspring"),sQuery(id+"F16.wireOp",EDGE,"E54.trimOffspring"),sQuery(id+"F16.wireOp",EDGE,"E55.trimOffspring"),sQuery(id+"F16.wireOp",EDGE,"E56.bottom"),sQuery(id+"F16.wireOp",EDGE,"E56.left"),sQuery(id+"F16.wireOp",EDGE,"E56.top"),sQuery(id+"F16.wireOp",EDGE,"E56.right"),sQuery(id+"F16.wireOp",EDGE,"E59"),sQuery(id+"F16.wireOp",EDGE,"E61"),sQuery(id+"F16.wireOp",EDGE,"E66.left"),sQuery(id+"F16.wireOp",EDGE,"E66.right"),sQuery(id+"F16.wireOp",EDGE,"E67.left"),sQuery(id+"F16.wireOp",EDGE,"E67.right"),sQuery(id+"F16.wireOp",EDGE,"E68.bottom"),sQuery(id+"F16.wireOp",EDGE,"E68.top"),sQuery(id+"F16.wireOp",EDGE,"E69.trimOffspring"),sQuery(id+"F16.wireOp",EDGE,"E70.trimOffspring"),sQuery(id+"F16.wireOp",EDGE,"E73.trimOffspring"),sQuery(id+"F16.wireOp",EDGE,"E74.trimOffspring"),sQuery(id+"F16.wireOp",EDGE,"E75.trimOffspring"),sQuery(id+"F16.wireOp",EDGE,"E77.trimOffspring"),sQuery(id+"F16.wireOp",EDGE,"E78.trimOffspring"),sQuery(id+"F16.wireOp",EDGE,"E80.trimOffspring"),sQuery(id+"F16.wireOp",EDGE,"E81.bottom"),sQuery(id+"F16.wireOp",EDGE,"E81.left"),sQuery(id+"F16.wireOp",EDGE,"E81.top"),sQuery(id+"F16.wireOp",EDGE,"E81.right"),sQuery(id+"F16.wireOp",EDGE,"E85"),sQuery(id+"F16.wireOp",EDGE,"E87"),sQuery(id+"F16.wireOp",EDGE,"E92.left"),sQuery(id+"F16.wireOp",EDGE,"E92.right"),sQuery(id+"F16.wireOp",EDGE,"E93.left"),sQuery(id+"F16.wireOp",EDGE,"E93.right"),sQuery(id+"F16.wireOp",EDGE,"E94.bottom"),sQuery(id+"F16.wireOp",EDGE,"E94.top"),sQuery(id+"F16.wireOp",EDGE,"E95.trimOffspring"),sQuery(id+"F16.wireOp",EDGE,"E96.trimOffspring"),sQuery(id+"F16.wireOp",EDGE,"E99.trimOffspring"),sQuery(id+"F16.wireOp",EDGE,"E100.trimOffspring"),sQuery(id+"F16.wireOp",EDGE,"E101.trimOffspring"),sQuery(id+"F16.wireOp",EDGE,"E103.trimOffspring"),sQuery(id+"F16.wireOp",EDGE,"E104.trimOffspring"),sQuery(id+"F16.wireOp",EDGE,"E106.trimOffspring"),sQuery(id+"F16.wireOp",EDGE,"E107.bottom"),sQuery(id+"F16.wireOp",EDGE,"E107.left"),sQuery(id+"F16.wireOp",EDGE,"E107.top"),sQuery(id+"F16.wireOp",EDGE,"E107.right"),sQuery(id+"F16.wireOp",EDGE,"E111"),sQuery(id+"F16.wireOp",EDGE,"E113"),sQuery(id+"F16.wireOp",EDGE,"E118.left"),sQuery(id+"F16.wireOp",EDGE,"E118.right"),sQuery(id+"F16.wireOp",EDGE,"E119.left"),sQuery(id+"F16.wireOp",EDGE,"E119.right"),sQuery(id+"F16.wireOp",EDGE,"E120.bottom"),sQuery(id+"F16.wireOp",EDGE,"E120.top"),sQuery(id+"F16.wireOp",EDGE,"E121.trimOffspring"),sQuery(id+"F16.wireOp",EDGE,"E122.trimOffspring"),sQuery(id+"F16.wireOp",EDGE,"E125.trimOffspring"),sQuery(id+"F16.wireOp",EDGE,"E126.trimOffspring"),sQuery(id+"F16.wireOp",EDGE,"E127.trimOffspring"),sQuery(id+"F16.wireOp",EDGE,"E129.trimOffspring"),sQuery(id+"F16.wireOp",EDGE,"E130.trimOffspring"),sQuery(id+"F16.wireOp",EDGE,"E132.trimOffspring"),sQuery(id+"F16.wireOp",EDGE,"E133.bottom"),sQuery(id+"F16.wireOp",EDGE,"E133.top"),sQuery(id+"F16.wireOp",EDGE,"E133.left"),sQuery(id+"F16.wireOp",EDGE,"E133.right")])],"isStart":false});
            var sketch = newSketch(context, id + "F22", { "sketchPlane" : qUnion([Q0])});
            skLineSegment(sketch, "E149.bottom", {"start": v(-94.98, -143.56) * mm, "end": v(-98.98, -143.56) * mm});
            skLineSegment(sketch, "E149.top", {"start": v(-94.98, -161.56) * mm, "end": v(-98.98, -161.56) * mm});
            skLineSegment(sketch, "E149.left", {"start": v(-94.98, -143.56) * mm, "end": v(-94.98, -161.56) * mm});
            skLineSegment(sketch, "E149.right", {"start": v(-98.98, -143.56) * mm, "end": v(-98.98, -161.56) * mm});
            skLineSegment(sketch, "E150.bottom", {"start": v(-76.98, -143.56) * mm, "end": v(-72.98, -143.56) * mm});
            skLineSegment(sketch, "E150.top", {"start": v(-76.98, -161.56) * mm, "end": v(-72.98, -161.56) * mm});
            skLineSegment(sketch, "E150.left", {"start": v(-76.98, -143.56) * mm, "end": v(-76.98, -161.56) * mm});
            skLineSegment(sketch, "E150.right", {"start": v(-72.98, -143.56) * mm, "end": v(-72.98, -161.56) * mm});
            skLineSegment(sketch, "E151.bottom", {"start": v(-64.98, -143.56) * mm, "end": v(-68.98, -143.56) * mm});
            skLineSegment(sketch, "E151.top", {"start": v(-64.98, -161.56) * mm, "end": v(-68.98, -161.56) * mm});
            skLineSegment(sketch, "E151.left", {"start": v(-64.98, -143.56) * mm, "end": v(-64.98, -161.56) * mm});
            skLineSegment(sketch, "E151.right", {"start": v(-68.98, -143.56) * mm, "end": v(-68.98, -161.56) * mm});
            skLineSegment(sketch, "E152.bottom", {"start": v(-46.98, -143.56) * mm, "end": v(-42.98, -143.56) * mm});
            skLineSegment(sketch, "E152.top", {"start": v(-46.98, -161.56) * mm, "end": v(-42.98, -161.56) * mm});
            skLineSegment(sketch, "E152.left", {"start": v(-46.98, -143.56) * mm, "end": v(-46.98, -161.56) * mm});
            skLineSegment(sketch, "E152.right", {"start": v(-42.98, -143.56) * mm, "end": v(-42.98, -161.56) * mm});
            skLineSegment(sketch, "E153.bottom", {"start": v(-34.98, -143.56) * mm, "end": v(-38.98, -143.56) * mm});
            skLineSegment(sketch, "E153.top", {"start": v(-34.98, -161.56) * mm, "end": v(-38.98, -161.56) * mm});
            skLineSegment(sketch, "E153.left", {"start": v(-34.98, -143.56) * mm, "end": v(-34.98, -161.56) * mm});
            skLineSegment(sketch, "E153.right", {"start": v(-38.98, -143.56) * mm, "end": v(-38.98, -161.56) * mm});
            skLineSegment(sketch, "E154.bottom", {"start": v(-16.98, -143.56) * mm, "end": v(-12.98, -143.56) * mm});
            skLineSegment(sketch, "E154.top", {"start": v(-16.98, -161.56) * mm, "end": v(-12.98, -161.56) * mm});
            skLineSegment(sketch, "E154.left", {"start": v(-16.98, -143.56) * mm, "end": v(-16.98, -161.56) * mm});
            skLineSegment(sketch, "E154.right", {"start": v(-12.98, -143.56) * mm, "end": v(-12.98, -161.56) * mm});
            skSolve(sketch);
        }
        {
            var Q0;
            Q0=qSketchRegion(id+"F22",true);
            extrude(context, id + "F23", {"entities" : qUnion([Q0]), "operationType" : NewBodyOperationType.ADD, "depth" : 3 * mm});
        }
        {
            var Q0;
            Q0=makeQuery(id+"F17.opExtrude","CAP_FACE",FACE,{"disambiguationData":[OSD([sQuery(id+"F16.wireOp",EDGE,"55227c07-3752-4080-a22d-609154aa437d.0"),sQuery(id+"F16.wireOp",EDGE,"55227c07-3752-4080-a22d-609154aa437d.1"),sQuery(id+"F16.wireOp",EDGE,"55227c07-3752-4080-a22d-609154aa437d.2"),sQuery(id+"F16.wireOp",EDGE,"55227c07-3752-4080-a22d-609154aa437d.3"),sQuery(id+"F16.wireOp",EDGE,"E36"),sQuery(id+"F16.wireOp",EDGE,"E38"),sQuery(id+"F16.wireOp",EDGE,"E43.left"),sQuery(id+"F16.wireOp",EDGE,"E43.right"),sQuery(id+"F16.wireOp",EDGE,"E44.left"),sQuery(id+"F16.wireOp",EDGE,"E44.right"),sQuery(id+"F16.wireOp",EDGE,"E45.bottom"),sQuery(id+"F16.wireOp",EDGE,"E45.top"),sQuery(id+"F16.wireOp",EDGE,"E46.trimOffspring"),sQuery(id+"F16.wireOp",EDGE,"E47.trimOffspring"),sQuery(id+"F16.wireOp",EDGE,"E50.trimOffspring"),sQuery(id+"F16.wireOp",EDGE,"E51.trimOffspring"),sQuery(id+"F16.wireOp",EDGE,"E52.trimOffspring"),sQuery(id+"F16.wireOp",EDGE,"E53.trimOffspring"),sQuery(id+"F16.wireOp",EDGE,"E54.trimOffspring"),sQuery(id+"F16.wireOp",EDGE,"E55.trimOffspring"),sQuery(id+"F16.wireOp",EDGE,"E56.bottom"),sQuery(id+"F16.wireOp",EDGE,"E56.left"),sQuery(id+"F16.wireOp",EDGE,"E56.top"),sQuery(id+"F16.wireOp",EDGE,"E56.right"),sQuery(id+"F16.wireOp",EDGE,"E59"),sQuery(id+"F16.wireOp",EDGE,"E61"),sQuery(id+"F16.wireOp",EDGE,"E66.left"),sQuery(id+"F16.wireOp",EDGE,"E66.right"),sQuery(id+"F16.wireOp",EDGE,"E67.left"),sQuery(id+"F16.wireOp",EDGE,"E67.right"),sQuery(id+"F16.wireOp",EDGE,"E68.bottom"),sQuery(id+"F16.wireOp",EDGE,"E68.top"),sQuery(id+"F16.wireOp",EDGE,"E69.trimOffspring"),sQuery(id+"F16.wireOp",EDGE,"E70.trimOffspring"),sQuery(id+"F16.wireOp",EDGE,"E73.trimOffspring"),sQuery(id+"F16.wireOp",EDGE,"E74.trimOffspring"),sQuery(id+"F16.wireOp",EDGE,"E75.trimOffspring"),sQuery(id+"F16.wireOp",EDGE,"E77.trimOffspring"),sQuery(id+"F16.wireOp",EDGE,"E78.trimOffspring"),sQuery(id+"F16.wireOp",EDGE,"E80.trimOffspring"),sQuery(id+"F16.wireOp",EDGE,"E81.bottom"),sQuery(id+"F16.wireOp",EDGE,"E81.left"),sQuery(id+"F16.wireOp",EDGE,"E81.top"),sQuery(id+"F16.wireOp",EDGE,"E81.right"),sQuery(id+"F16.wireOp",EDGE,"E85"),sQuery(id+"F16.wireOp",EDGE,"E87"),sQuery(id+"F16.wireOp",EDGE,"E92.left"),sQuery(id+"F16.wireOp",EDGE,"E92.right"),sQuery(id+"F16.wireOp",EDGE,"E93.left"),sQuery(id+"F16.wireOp",EDGE,"E93.right"),sQuery(id+"F16.wireOp",EDGE,"E94.bottom"),sQuery(id+"F16.wireOp",EDGE,"E94.top"),sQuery(id+"F16.wireOp",EDGE,"E95.trimOffspring"),sQuery(id+"F16.wireOp",EDGE,"E96.trimOffspring"),sQuery(id+"F16.wireOp",EDGE,"E99.trimOffspring"),sQuery(id+"F16.wireOp",EDGE,"E100.trimOffspring"),sQuery(id+"F16.wireOp",EDGE,"E101.trimOffspring"),sQuery(id+"F16.wireOp",EDGE,"E103.trimOffspring"),sQuery(id+"F16.wireOp",EDGE,"E104.trimOffspring"),sQuery(id+"F16.wireOp",EDGE,"E106.trimOffspring"),sQuery(id+"F16.wireOp",EDGE,"E107.bottom"),sQuery(id+"F16.wireOp",EDGE,"E107.left"),sQuery(id+"F16.wireOp",EDGE,"E107.top"),sQuery(id+"F16.wireOp",EDGE,"E107.right"),sQuery(id+"F16.wireOp",EDGE,"E111"),sQuery(id+"F16.wireOp",EDGE,"E113"),sQuery(id+"F16.wireOp",EDGE,"E118.left"),sQuery(id+"F16.wireOp",EDGE,"E118.right"),sQuery(id+"F16.wireOp",EDGE,"E119.left"),sQuery(id+"F16.wireOp",EDGE,"E119.right"),sQuery(id+"F16.wireOp",EDGE,"E120.bottom"),sQuery(id+"F16.wireOp",EDGE,"E120.top"),sQuery(id+"F16.wireOp",EDGE,"E121.trimOffspring"),sQuery(id+"F16.wireOp",EDGE,"E122.trimOffspring"),sQuery(id+"F16.wireOp",EDGE,"E125.trimOffspring"),sQuery(id+"F16.wireOp",EDGE,"E126.trimOffspring"),sQuery(id+"F16.wireOp",EDGE,"E127.trimOffspring"),sQuery(id+"F16.wireOp",EDGE,"E129.trimOffspring"),sQuery(id+"F16.wireOp",EDGE,"E130.trimOffspring"),sQuery(id+"F16.wireOp",EDGE,"E132.trimOffspring"),sQuery(id+"F16.wireOp",EDGE,"E133.bottom"),sQuery(id+"F16.wireOp",EDGE,"E133.top"),sQuery(id+"F16.wireOp",EDGE,"E133.left"),sQuery(id+"F16.wireOp",EDGE,"E133.right")])],"isStart":false});
            var sketch = newSketch(context, id + "F24", { "sketchPlane" : qUnion([Q0])});
            skLineSegment(sketch, "E155.bottom", {"start": v(-98.98, -143.56) * mm, "end": v(-72.98, -143.56) * mm});
            skLineSegment(sketch, "E155.top", {"start": v(-98.98, -134.06) * mm, "end": v(-72.98, -134.06) * mm});
            skLineSegment(sketch, "E155.left", {"start": v(-98.98, -143.56) * mm, "end": v(-98.98, -134.06) * mm});
            skLineSegment(sketch, "E155.right", {"start": v(-72.98, -143.56) * mm, "end": v(-72.98, -134.06) * mm});
            skLineSegment(sketch, "E156.bottom", {"start": v(-98.98, -161.56) * mm, "end": v(-72.98, -161.56) * mm});
            skLineSegment(sketch, "E156.top", {"start": v(-98.98, -171.06) * mm, "end": v(-72.98, -171.06) * mm});
            skLineSegment(sketch, "E156.left", {"start": v(-98.98, -161.56) * mm, "end": v(-98.98, -171.06) * mm});
            skLineSegment(sketch, "E156.right", {"start": v(-72.98, -161.56) * mm, "end": v(-72.98, -171.06) * mm});
            skCircle(sketch, "E157", {"center": v(-85.98, -137.56) * mm, "radius": 1.5 * mm});
            skCircle(sketch, "E158", {"center": v(-85.98, -167.56) * mm, "radius": 1.5 * mm});
            skLineSegment(sketch, "E159.bottom", {"start": v(-68.98, -143.56) * mm, "end": v(-42.98, -143.56) * mm});
            skLineSegment(sketch, "E159.top", {"start": v(-68.98, -134.06) * mm, "end": v(-42.98, -134.06) * mm});
            skLineSegment(sketch, "E159.left", {"start": v(-68.98, -143.56) * mm, "end": v(-68.98, -134.06) * mm});
            skLineSegment(sketch, "E159.right", {"start": v(-42.98, -143.56) * mm, "end": v(-42.98, -134.06) * mm});
            skLineSegment(sketch, "E160.bottom", {"start": v(-68.98, -161.56) * mm, "end": v(-42.98, -161.56) * mm});
            skLineSegment(sketch, "E160.top", {"start": v(-68.98, -171.06) * mm, "end": v(-42.98, -171.06) * mm});
            skLineSegment(sketch, "E160.left", {"start": v(-68.98, -161.56) * mm, "end": v(-68.98, -171.06) * mm});
            skLineSegment(sketch, "E160.right", {"start": v(-42.98, -161.56) * mm, "end": v(-42.98, -171.06) * mm});
            skLineSegment(sketch, "E161.bottom", {"start": v(-38.98, -143.56) * mm, "end": v(-12.98, -143.56) * mm});
            skLineSegment(sketch, "E161.top", {"start": v(-38.98, -134.06) * mm, "end": v(-12.98, -134.06) * mm});
            skLineSegment(sketch, "E161.left", {"start": v(-38.98, -143.56) * mm, "end": v(-38.98, -134.06) * mm});
            skLineSegment(sketch, "E161.right", {"start": v(-12.98, -143.56) * mm, "end": v(-12.98, -134.06) * mm});
            skLineSegment(sketch, "E162.bottom", {"start": v(-38.98, -161.56) * mm, "end": v(-12.98, -161.56) * mm});
            skLineSegment(sketch, "E162.top", {"start": v(-38.98, -171.06) * mm, "end": v(-12.98, -171.06) * mm});
            skLineSegment(sketch, "E162.left", {"start": v(-38.98, -161.56) * mm, "end": v(-38.98, -171.06) * mm});
            skLineSegment(sketch, "E162.right", {"start": v(-12.98, -161.56) * mm, "end": v(-12.98, -171.06) * mm});
            skCircle(sketch, "E163", {"center": v(-55.98, -137.56) * mm, "radius": 1.5 * mm});
            skCircle(sketch, "E164", {"center": v(-55.98, -167.56) * mm, "radius": 1.5 * mm});
            skCircle(sketch, "E165", {"center": v(-25.98, -137.56) * mm, "radius": 1.5 * mm});
            skCircle(sketch, "E166", {"center": v(-25.98, -167.56) * mm, "radius": 1.5 * mm});
            skSolve(sketch);
        }
        {
            var Q0;
            Q0=makeQuery(id+"F22.imprint","IMPRINT",FACE,{"disambiguationData":[TD([[makeQuery(id+"F22.imprint","IMPRINT",EDGE,{"derivedFrom":sQuery(id+"F22.wireOp",EDGE,"E149.bottom")}),-1.0]])]});
            var sketch = newSketch(context, id + "F25", { "sketchPlane" : qUnion([Q0])});
            skLineSegment(sketch, "E167.bottom", {"start": v(-124.73, -151.56) * mm, "end": v(-121.73, -151.56) * mm});
            skLineSegment(sketch, "E167.top", {"start": v(-124.73, -153.56) * mm, "end": v(-121.73, -153.56) * mm});
            skLineSegment(sketch, "E167.left", {"start": v(-124.73, -151.56) * mm, "end": v(-124.73, -153.56) * mm});
            skLineSegment(sketch, "E167.right", {"start": v(-121.73, -151.56) * mm, "end": v(-121.73, -153.56) * mm});
            skLineSegment(sketch, "E168.bottom", {"start": v(-110.23, -151.56) * mm, "end": v(-107.23, -151.56) * mm});
            skLineSegment(sketch, "E168.top", {"start": v(-110.23, -153.56) * mm, "end": v(-107.23, -153.56) * mm});
            skLineSegment(sketch, "E168.left", {"start": v(-110.23, -151.56) * mm, "end": v(-110.23, -153.56) * mm});
            skLineSegment(sketch, "E168.right", {"start": v(-107.23, -151.56) * mm, "end": v(-107.23, -153.56) * mm});
            skSolve(sketch);
        }
        {
            var Q0;
            Q0=qSketchRegion(id+"F25",true);
            extrude(context, id + "F26", {"entities" : qUnion([Q0]), "operationType" : NewBodyOperationType.ADD, "depth" : 9 * mm});
        }
        {
            var Q0;
            Q0=makeQuery(id+"F22.imprint","IMPRINT",FACE,{"disambiguationData":[TD([[makeQuery(id+"F22.imprint","IMPRINT",EDGE,{"derivedFrom":sQuery(id+"F22.wireOp",EDGE,"E149.bottom")}),-1.0]])]});
            var sketch = newSketch(context, id + "F27", { "sketchPlane" : qUnion([Q0])});
            skLineSegment(sketch, "E169.bottom", {"start": v(-118.48, -151.56) * mm, "end": v(-113.48, -151.56) * mm});
            skLineSegment(sketch, "E169.top", {"start": v(-118.48, -153.56) * mm, "end": v(-113.48, -153.56) * mm});
            skLineSegment(sketch, "E169.left", {"start": v(-118.48, -151.56) * mm, "end": v(-118.48, -153.56) * mm});
            skLineSegment(sketch, "E169.right", {"start": v(-113.48, -151.56) * mm, "end": v(-113.48, -153.56) * mm});
            skSolve(sketch);
        }
        {
            var Q0;
            Q0=qSketchRegion(id+"F27",true);
            extrude(context, id + "F28", {"entities" : qUnion([Q0]), "operationType" : NewBodyOperationType.ADD, "depth" : 3 * mm});
        }
        {
            var Q0;
            Q0=makeQuery(id+"F19.opExtrude","SWEPT_EDGE",EDGE,{"disambiguationData":[OSD([sQuery(id+"F18.wireOp",EDGE,"E134.bottom"),sQuery(id+"F18.wireOp",EDGE,"E134.left")])]});
            var Q1;
            Q1=makeQuery(id+"F19.opExtrude","SWEPT_EDGE",EDGE,{"disambiguationData":[OSD([sQuery(id+"F18.wireOp",EDGE,"E134.top"),sQuery(id+"F18.wireOp",EDGE,"E134.left")])]});
            var Q2;
            Q2=makeQuery(id+"F19.opExtrude","SWEPT_EDGE",EDGE,{"disambiguationData":[OSD([sQuery(id+"F18.wireOp",EDGE,"E134.top"),sQuery(id+"F18.wireOp",EDGE,"E134.right")])]});
            var Q3;
            Q3=makeQuery(id+"F19.opExtrude","SWEPT_EDGE",EDGE,{"disambiguationData":[OSD([sQuery(id+"F18.wireOp",EDGE,"E134.bottom"),sQuery(id+"F18.wireOp",EDGE,"E134.right")])]});
            var Q4;
            Q4=makeQuery(id+"F19.opExtrude","CAP_EDGE",EDGE,{"disambiguationData":[OSD([sQuery(id+"F18.wireOp",EDGE,"E134.top")])],"isStart":false});
            var Q5;
            Q5=makeQuery(id+"F19.opExtrude","CAP_EDGE",EDGE,{"disambiguationData":[OSD([sQuery(id+"F18.wireOp",EDGE,"E134.left")])],"isStart":false});
            var Q6;
            Q6=makeQuery(id+"F19.opExtrude","CAP_EDGE",EDGE,{"disambiguationData":[OSD([sQuery(id+"F18.wireOp",EDGE,"E134.bottom")])],"isStart":false});
            var Q7;
            Q7=makeQuery(id+"F19.opExtrude","CAP_EDGE",EDGE,{"disambiguationData":[OSD([sQuery(id+"F18.wireOp",EDGE,"E134.right")])],"isStart":false});
            fillet(context, id + "F29", {"entities" : qUnion([Q0, Q1, Q2, Q3, Q4, Q5, Q6, Q7]), "radius" : 1 * mm, "tangentPropagation" : true, "allowEdgeOverflow" : false});
        }
        {
            var Q0;
            Q0=makeQuery(id+"F8.opExtrude","SWEPT_EDGE",EDGE,{"disambiguationData":[OSD([sQuery(id+"F7.wireOp",EDGE,"E14.top"),sQuery(id+"F7.wireOp",EDGE,"E14.right")])]});
            var Q1;
            Q1=makeQuery(id+"F8.opExtrude","CAP_EDGE",EDGE,{"disambiguationData":[OSD([sQuery(id+"F7.wireOp",EDGE,"E14.top")])],"isStart":false});
            var Q2;
            Q2=makeQuery(id+"F8.opExtrude","CAP_EDGE",EDGE,{"disambiguationData":[OSD([sQuery(id+"F7.wireOp",EDGE,"E14.right")])],"isStart":false});
            var Q3;
            Q3=makeQuery(id+"F8.opExtrude","SWEPT_EDGE",EDGE,{"disambiguationData":[OSD([sQuery(id+"F7.wireOp",EDGE,"E14.bottom"),sQuery(id+"F7.wireOp",EDGE,"E14.right")])]});
            var Q4;
            Q4=makeQuery(id+"F8.opExtrude","CAP_EDGE",EDGE,{"disambiguationData":[OSD([sQuery(id+"F7.wireOp",EDGE,"E14.bottom")])],"isStart":false});
            var Q5;
            Q5=makeQuery(id+"F8.opExtrude","SWEPT_EDGE",EDGE,{"disambiguationData":[OSD([sQuery(id+"F7.wireOp",EDGE,"E14.bottom"),sQuery(id+"F7.wireOp",EDGE,"E14.left")])]});
            var Q6;
            Q6=makeQuery(id+"F8.opExtrude","CAP_EDGE",EDGE,{"disambiguationData":[OSD([sQuery(id+"F7.wireOp",EDGE,"E14.left")])],"isStart":false});
            var Q7;
            Q7=makeQuery(id+"F8.opExtrude","SWEPT_EDGE",EDGE,{"disambiguationData":[OSD([sQuery(id+"F7.wireOp",EDGE,"E14.top"),sQuery(id+"F7.wireOp",EDGE,"E14.left")])]});
            var Q8;
            Q8=makeQuery(id+"F1.opExtrude","SWEPT_EDGE",EDGE,{"disambiguationData":[OSD([sQuery(id+"F0.wireOp",EDGE,"E1.bottom"),sQuery(id+"F0.wireOp",EDGE,"E1.right")])]});
            var Q9;
            Q9=makeQuery(id+"F1.opExtrude","CAP_EDGE",EDGE,{"disambiguationData":[OSD([sQuery(id+"F0.wireOp",EDGE,"E1.bottom")])],"isStart":false});
            var Q10;
            Q10=makeQuery(id+"F1.opExtrude","SWEPT_EDGE",EDGE,{"disambiguationData":[OSD([sQuery(id+"F0.wireOp",EDGE,"E1.bottom"),sQuery(id+"F0.wireOp",EDGE,"E1.left")])]});
            var Q11;
            Q11=makeQuery(id+"F1.opExtrude","CAP_EDGE",EDGE,{"disambiguationData":[OSD([sQuery(id+"F0.wireOp",EDGE,"E1.right")])],"isStart":false});
            var Q12;
            Q12=makeQuery(id+"F1.opExtrude","SWEPT_EDGE",EDGE,{"disambiguationData":[OSD([sQuery(id+"F0.wireOp",EDGE,"E1.top"),sQuery(id+"F0.wireOp",EDGE,"E1.right")])]});
            var Q13;
            Q13=makeQuery(id+"F1.opExtrude","CAP_EDGE",EDGE,{"disambiguationData":[OSD([sQuery(id+"F0.wireOp",EDGE,"E1.top")])],"isStart":false});
            var Q14;
            Q14=makeQuery(id+"F1.opExtrude","SWEPT_EDGE",EDGE,{"disambiguationData":[OSD([sQuery(id+"F0.wireOp",EDGE,"E1.top"),sQuery(id+"F0.wireOp",EDGE,"E1.left")])]});
            var Q15;
            Q15=makeQuery(id+"F1.opExtrude","CAP_EDGE",EDGE,{"disambiguationData":[OSD([sQuery(id+"F0.wireOp",EDGE,"E1.left")])],"isStart":false});
            fillet(context, id + "F30", {"entities" : qUnion([Q0, Q1, Q2, Q3, Q4, Q5, Q6, Q7, Q8, Q9, Q10, Q11, Q12, Q13, Q14, Q15]), "radius" : 0.5 * mm, "tangentPropagation" : true, "allowEdgeOverflow" : false});
        }
        {
            var Q0;
            Q0=makeQuery(id+"F24.imprint","IMPRINT",FACE,{"disambiguationData":[TD([[makeQuery(id+"F24.imprint","IMPRINT",EDGE,{"derivedFrom":sQuery(id+"F24.wireOp",EDGE,"E155.top")}),-1.0]])]});
            var Q1;
            Q1=makeQuery(id+"F24.imprint","IMPRINT",FACE,{"disambiguationData":[TD([[makeQuery(id+"F24.imprint","IMPRINT",EDGE,{"derivedFrom":sQuery(id+"F24.wireOp",EDGE,"E156.top")}),1.0]])]});
            var Q2;
            Q2=makeQuery(id+"F24.imprint","IMPRINT",FACE,{"disambiguationData":[TD([[makeQuery(id+"F24.imprint","IMPRINT",EDGE,{"derivedFrom":sQuery(id+"F24.wireOp",EDGE,"E160.top")}),1.0]])]});
            var Q3;
            Q3=makeQuery(id+"F24.imprint","IMPRINT",FACE,{"disambiguationData":[TD([[makeQuery(id+"F24.imprint","IMPRINT",EDGE,{"derivedFrom":sQuery(id+"F24.wireOp",EDGE,"E159.top")}),-1.0]])]});
            var Q4;
            Q4=makeQuery(id+"F24.imprint","IMPRINT",FACE,{"disambiguationData":[TD([[makeQuery(id+"F24.imprint","IMPRINT",EDGE,{"derivedFrom":sQuery(id+"F24.wireOp",EDGE,"E161.top")}),-1.0]])]});
            var Q5;
            Q5=makeQuery(id+"F24.imprint","IMPRINT",FACE,{"disambiguationData":[TD([[makeQuery(id+"F24.imprint","IMPRINT",EDGE,{"derivedFrom":sQuery(id+"F24.wireOp",EDGE,"E162.top")}),1.0]])]});
            extrude(context, id + "F31", {"entities" : qUnion([Q0, Q1, Q2, Q3, Q4, Q5]), "operationType" : NewBodyOperationType.ADD, "depth" : 3 * mm});
        }
        {
            var Q0;
            Q0=makeQuery(id+"F17.opExtrude","SWEPT_FACE",FACE,{"disambiguationData":[OSD([sQuery(id+"F16.wireOp",EDGE,"E133.left")])]});
            extrude(context, id + "F32", {"entities" : qUnion([Q0]), "operationType" : NewBodyOperationType.ADD, "depth" : 2 * mm});
        }
        {
            var Q0;
            {var subQ0=sQuery(id+"F16.wireOp",EDGE,"E133.left");var subQ1=sQuery(id+"F16.wireOp",EDGE,"55227c07-3752-4080-a22d-609154aa437d.3");var subQ2=sQuery(id+"F16.wireOp",EDGE,"55227c07-3752-4080-a22d-609154aa437d.0");var subQ4=sQuery(id+"F16.wireOp",EDGE,"E54.trimOffspring");var subQ6=sQuery(id+"F16.wireOp",EDGE,"E133.top");var subQ7=sQuery(id+"F16.wireOp",EDGE,"E55.trimOffspring");var subQ8=sQuery(id+"F16.wireOp",EDGE,"55227c07-3752-4080-a22d-609154aa437d.2");var subQ11=sQuery(id+"F16.wireOp",EDGE,"E53.trimOffspring");var subQ13=sQuery(id+"F16.wireOp",EDGE,"E133.bottom");var subQ14=sQuery(id+"F16.wireOp",EDGE,"E47.trimOffspring");var subQ16=sQuery(id+"F16.wireOp",EDGE,"E52.trimOffspring");var subQ17=sQuery(id+"F16.wireOp",EDGE,"E51.trimOffspring");var subQ18=sQuery(id+"F16.wireOp",EDGE,"55227c07-3752-4080-a22d-609154aa437d.1");var subQ21=sQuery(id+"F16.wireOp",EDGE,"E45.bottom");var subQ22=sQuery(id+"F16.wireOp",EDGE,"E44.right");var subQ24=sQuery(id+"F16.wireOp",EDGE,"E43.right");var subQ26=sQuery(id+"F16.wireOp",EDGE,"E44.left");var subQ28=sQuery(id+"F16.wireOp",EDGE,"E46.trimOffspring");var subQ29=sQuery(id+"F16.wireOp",EDGE,"E45.top");var subQ30=sQuery(id+"F16.wireOp",EDGE,"E43.left");var subQ31=sQuery(id+"F16.wireOp",EDGE,"E36");var subQ32=sQuery(id+"F16.wireOp",EDGE,"E38");var subQ33=sQuery(id+"F16.wireOp",EDGE,"E50.trimOffspring");Q0=makeQuery(id+"F32.boolean.opBoolean","MERGE",FACE,{"derivedFrom":[makeQuery(id+"F31.boolean.opBoolean","SPLIT",FACE,{"disambiguationData":[TD([makeQuery(id+"F17.opExtrude","SWEPT_FACE",FACE,{"disambiguationData":[OSD([subQ31])]})])],"derivedFrom":makeQuery(id+"F17.opExtrude","CAP_FACE",FACE,{"disambiguationData":[OSD([subQ2,subQ18,subQ8,subQ1,subQ31,subQ32,subQ30,subQ24,subQ26,subQ22,subQ21,subQ29,subQ28,subQ14,subQ33,subQ17,subQ16,subQ11,subQ4,subQ7,sQuery(id+"F16.wireOp",EDGE,"E56.bottom"),sQuery(id+"F16.wireOp",EDGE,"E56.left"),sQuery(id+"F16.wireOp",EDGE,"E56.top"),sQuery(id+"F16.wireOp",EDGE,"E56.right"),sQuery(id+"F16.wireOp",EDGE,"E59"),sQuery(id+"F16.wireOp",EDGE,"E61"),sQuery(id+"F16.wireOp",EDGE,"E66.left"),sQuery(id+"F16.wireOp",EDGE,"E66.right"),sQuery(id+"F16.wireOp",EDGE,"E67.left"),sQuery(id+"F16.wireOp",EDGE,"E67.right"),sQuery(id+"F16.wireOp",EDGE,"E68.bottom"),sQuery(id+"F16.wireOp",EDGE,"E68.top"),sQuery(id+"F16.wireOp",EDGE,"E69.trimOffspring"),sQuery(id+"F16.wireOp",EDGE,"E70.trimOffspring"),sQuery(id+"F16.wireOp",EDGE,"E73.trimOffspring"),sQuery(id+"F16.wireOp",EDGE,"E74.trimOffspring"),sQuery(id+"F16.wireOp",EDGE,"E75.trimOffspring"),sQuery(id+"F16.wireOp",EDGE,"E77.trimOffspring"),sQuery(id+"F16.wireOp",EDGE,"E78.trimOffspring"),sQuery(id+"F16.wireOp",EDGE,"E80.trimOffspring"),sQuery(id+"F16.wireOp",EDGE,"E81.bottom"),sQuery(id+"F16.wireOp",EDGE,"E81.left"),sQuery(id+"F16.wireOp",EDGE,"E81.top"),sQuery(id+"F16.wireOp",EDGE,"E81.right"),sQuery(id+"F16.wireOp",EDGE,"E85"),sQuery(id+"F16.wireOp",EDGE,"E87"),sQuery(id+"F16.wireOp",EDGE,"E92.left"),sQuery(id+"F16.wireOp",EDGE,"E92.right"),sQuery(id+"F16.wireOp",EDGE,"E93.left"),sQuery(id+"F16.wireOp",EDGE,"E93.right"),sQuery(id+"F16.wireOp",EDGE,"E94.bottom"),sQuery(id+"F16.wireOp",EDGE,"E94.top"),sQuery(id+"F16.wireOp",EDGE,"E95.trimOffspring"),sQuery(id+"F16.wireOp",EDGE,"E96.trimOffspring"),sQuery(id+"F16.wireOp",EDGE,"E99.trimOffspring"),sQuery(id+"F16.wireOp",EDGE,"E100.trimOffspring"),sQuery(id+"F16.wireOp",EDGE,"E101.trimOffspring"),sQuery(id+"F16.wireOp",EDGE,"E103.trimOffspring"),sQuery(id+"F16.wireOp",EDGE,"E104.trimOffspring"),sQuery(id+"F16.wireOp",EDGE,"E106.trimOffspring"),sQuery(id+"F16.wireOp",EDGE,"E107.bottom"),sQuery(id+"F16.wireOp",EDGE,"E107.left"),sQuery(id+"F16.wireOp",EDGE,"E107.top"),sQuery(id+"F16.wireOp",EDGE,"E107.right"),sQuery(id+"F16.wireOp",EDGE,"E111"),sQuery(id+"F16.wireOp",EDGE,"E113"),sQuery(id+"F16.wireOp",EDGE,"E118.left"),sQuery(id+"F16.wireOp",EDGE,"E118.right"),sQuery(id+"F16.wireOp",EDGE,"E119.left"),sQuery(id+"F16.wireOp",EDGE,"E119.right"),sQuery(id+"F16.wireOp",EDGE,"E120.bottom"),sQuery(id+"F16.wireOp",EDGE,"E120.top"),sQuery(id+"F16.wireOp",EDGE,"E121.trimOffspring"),sQuery(id+"F16.wireOp",EDGE,"E122.trimOffspring"),sQuery(id+"F16.wireOp",EDGE,"E125.trimOffspring"),sQuery(id+"F16.wireOp",EDGE,"E126.trimOffspring"),sQuery(id+"F16.wireOp",EDGE,"E127.trimOffspring"),sQuery(id+"F16.wireOp",EDGE,"E129.trimOffspring"),sQuery(id+"F16.wireOp",EDGE,"E130.trimOffspring"),sQuery(id+"F16.wireOp",EDGE,"E132.trimOffspring"),subQ13,subQ6,subQ0,sQuery(id+"F16.wireOp",EDGE,"E133.right")])],"isStart":false})}),makeQuery(id+"F32.opExtrude","SWEPT_FACE",FACE,{"disambiguationData":[OSD([subQ0]),TDD([makeQuery(id+"F17.opExtrude","CAP_EDGE",EDGE,{"disambiguationData":[OSD([subQ0])],"isStart":false})])]})]});}
            var sketch = newSketch(context, id + "F33", { "sketchPlane" : qUnion([Q0])});
            skLineSegment(sketch, "E170.bottom", {"start": v(-131.58, -134.06) * mm, "end": v(-129.58, -134.06) * mm});
            skLineSegment(sketch, "E170.top", {"start": v(-131.58, -171.06) * mm, "end": v(-129.58, -171.06) * mm});
            skLineSegment(sketch, "E170.left", {"start": v(-131.58, -134.06) * mm, "end": v(-131.58, -171.06) * mm});
            skLineSegment(sketch, "E170.right", {"start": v(-129.58, -134.06) * mm, "end": v(-129.58, -171.06) * mm});
            skSolve(sketch);
        }
        {
            var Q0;
            Q0=qSketchRegion(id+"F33",true);
            extrude(context, id + "F34", {"entities" : qUnion([Q0]), "operationType" : NewBodyOperationType.ADD, "depth" : 7 * mm});
        }
        {
            var Q0;
            Q0=makeQuery(id+"F21.boolean.opBoolean","COPY",FACE,{"derivedFrom":makeQuery(id+"F21.opExtrude","CAP_FACE",FACE,{"disambiguationData":[OSD([sQuery(id+"F20.wireOp",EDGE,"E148.bottom"),sQuery(id+"F20.wireOp",EDGE,"E148.top"),sQuery(id+"F20.wireOp",EDGE,"E148.left"),sQuery(id+"F20.wireOp",EDGE,"E148.right")])],"isStart":false})});
            var sketch = newSketch(context, id + "F35", { "sketchPlane" : qUnion([Q0])});
            skLineSegment(sketch, "E171.bottom", {"start": v(22.06, 164.66) * mm, "end": v(42.46, 164.66) * mm});
            skLineSegment(sketch, "E171.top", {"start": v(22.06, 173.06) * mm, "end": v(42.46, 173.06) * mm});
            skLineSegment(sketch, "E171.left", {"start": v(22.06, 164.66) * mm, "end": v(22.06, 173.06) * mm});
            skLineSegment(sketch, "E171.right", {"start": v(42.46, 164.66) * mm, "end": v(42.46, 173.06) * mm});
            skLineSegment(sketch, "E172.bottom", {"start": v(22.06, 144.26) * mm, "end": v(42.46, 144.26) * mm});
            skLineSegment(sketch, "E172.top", {"start": v(22.06, 135.86) * mm, "end": v(42.46, 135.86) * mm});
            skLineSegment(sketch, "E172.left", {"start": v(22.06, 144.26) * mm, "end": v(22.06, 135.86) * mm});
            skLineSegment(sketch, "E172.right", {"start": v(42.46, 144.26) * mm, "end": v(42.46, 135.86) * mm});
            skSolve(sketch);
        }
        {
            var Q0;
            Q0=qSketchRegion(id+"F35",true);
            extrude(context, id + "F36", {"entities" : qUnion([Q0]), "operationType" : NewBodyOperationType.ADD, "depth" : 3 * mm});
        }
        {
            var Q0;
            Q0=makeQuery(id+"F19.opExtrude","SWEPT_FACE",FACE,{"disambiguationData":[OSD([sQuery(id+"F18.wireOp",EDGE,"E134.left")])]});
            var sketch = newSketch(context, id + "F37", { "sketchPlane" : qUnion([Q0])});
            skCircle(sketch, "E173", {"center": v(139.86, 5.5) * mm, "radius": 1.5 * mm});
            skCircle(sketch, "E174", {"center": v(169.06, 5.5) * mm, "radius": 1.5 * mm});
            skSolve(sketch);
        }
        {
            var Q0;
            Q0=qSketchRegion(id+"F37",true);
            extrude(context, id + "F38", {"entities" : qUnion([Q0]), "operationType" : NewBodyOperationType.REMOVE, "oppositeDirection" : true, "depth" : 3 * mm});
        }
        {
            var Q0;
            Q0=makeQuery(id+"F34.boolean.opBoolean","MERGE",FACE,{"derivedFrom":[makeQuery(id+"F32.opExtrude","CAP_FACE",FACE,{"disambiguationData":[OSD([sQuery(id+"F16.wireOp",EDGE,"E133.left")])],"isStart":false}),makeQuery(id+"F34.opExtrude","SWEPT_FACE",FACE,{"disambiguationData":[OSD([sQuery(id+"F33.wireOp",EDGE,"E170.left")])]})]});
            var sketch = newSketch(context, id + "F39", { "sketchPlane" : qUnion([Q0])});
            skCircle(sketch, "E175", {"center": v(137.96, 5.5) * mm, "radius": 1.2 * mm});
            skCircle(sketch, "E176", {"center": v(167.16, 5.5) * mm, "radius": 1.2 * mm});
            skSolve(sketch);
        }
        {
            var Q0;
            Q0=makeQuery(id+"F19.opExtrude","SWEPT_FACE",FACE,{"disambiguationData":[OSD([sQuery(id+"F18.wireOp",EDGE,"E134.right")])]});
            var sketch = newSketch(context, id + "F40", { "sketchPlane" : qUnion([Q0])});
            skCircle(sketch, "E177", {"center": v(-169.06, 5.5) * mm, "radius": 1.5 * mm});
            skCircle(sketch, "E178", {"center": v(-139.86, 5.5) * mm, "radius": 1.5 * mm});
            skSolve(sketch);
        }
        {
            var Q0;
            Q0=makeQuery(id+"F40.imprint","IMPRINT",FACE,{"disambiguationData":[TD([[makeQuery(id+"F40.imprint","IMPRINT",EDGE,{"derivedFrom":sQuery(id+"F40.wireOp",EDGE,"E177")}),1.0]])]});
            var Q1;
            Q1=makeQuery(id+"F40.imprint","IMPRINT",FACE,{"disambiguationData":[TD([[makeQuery(id+"F40.imprint","IMPRINT",EDGE,{"derivedFrom":sQuery(id+"F40.wireOp",EDGE,"E178")}),1.0]])]});
            extrude(context, id + "F41", {"entities" : qUnion([Q0, Q1]), "operationType" : NewBodyOperationType.REMOVE, "oppositeDirection" : true, "depth" : 2 * mm});
        }
        {
            var Q0;
            {var subQ0=sQuery(id+"F20.wireOp",EDGE,"E148.top");var subQ1=sQuery(id+"F20.wireOp",EDGE,"E148.bottom");var subQ2=sQuery(id+"F20.wireOp",EDGE,"E148.right");Q0=makeQuery(id+"F36.boolean.opBoolean","SPLIT",FACE,{"disambiguationData":[TD([makeQuery(id+"F19.opExtrude","SWEPT_FACE",FACE,{"disambiguationData":[OSD([sQuery(id+"F18.wireOp",EDGE,"E135.right")])]})])],"derivedFrom":makeQuery(id+"F21.boolean.opBoolean","COPY",FACE,{"derivedFrom":makeQuery(id+"F21.opExtrude","CAP_FACE",FACE,{"disambiguationData":[OSD([subQ1,subQ0,sQuery(id+"F20.wireOp",EDGE,"E148.left"),subQ2])],"isStart":false})})});}
            var sketch = newSketch(context, id + "F42", { "sketchPlane" : qUnion([Q0])});
            skLineSegment(sketch, "E179.bottom", {"start": v(45.96, 173.06) * mm, "end": v(48.96, 173.06) * mm});
            skLineSegment(sketch, "E179.top", {"start": v(45.96, 135.86) * mm, "end": v(48.96, 135.86) * mm});
            skLineSegment(sketch, "E179.left", {"start": v(45.96, 173.06) * mm, "end": v(45.96, 135.86) * mm});
            skLineSegment(sketch, "E179.right", {"start": v(48.96, 173.06) * mm, "end": v(48.96, 135.86) * mm});
            skLineSegment(sketch, "E180.bottom", {"start": v(75.86, 173.06) * mm, "end": v(78.86, 173.06) * mm});
            skLineSegment(sketch, "E180.top", {"start": v(75.86, 135.86) * mm, "end": v(78.86, 135.86) * mm});
            skLineSegment(sketch, "E180.left", {"start": v(75.86, 173.06) * mm, "end": v(75.86, 135.86) * mm});
            skLineSegment(sketch, "E180.right", {"start": v(78.86, 173.06) * mm, "end": v(78.86, 135.86) * mm});
            skLineSegment(sketch, "E181.bottom", {"start": v(105.86, 173.06) * mm, "end": v(108.86, 173.06) * mm});
            skLineSegment(sketch, "E181.top", {"start": v(105.86, 135.86) * mm, "end": v(108.86, 135.86) * mm});
            skLineSegment(sketch, "E181.left", {"start": v(105.86, 173.06) * mm, "end": v(105.86, 135.86) * mm});
            skLineSegment(sketch, "E181.right", {"start": v(108.86, 173.06) * mm, "end": v(108.86, 135.86) * mm});
            skSolve(sketch);
        }
        {
            var Q0;
            Q0=qSketchRegion(id+"F42",true);
            extrude(context, id + "F43", {"entities" : qUnion([Q0]), "operationType" : NewBodyOperationType.ADD, "depth" : 1 * mm});
        }
        {
            var Q0;
            Q0=makeQuery(id+"F31.boolean.opBoolean","MERGE",FACE,{"derivedFrom":[makeQuery(id+"F23.opExtrude","SWEPT_FACE",FACE,{"disambiguationData":[OSD([sQuery(id+"F22.wireOp",EDGE,"E154.right")])]}),makeQuery(id+"F31.opExtrude","SWEPT_FACE",FACE,{"disambiguationData":[OSD([sQuery(id+"F24.wireOp",EDGE,"E161.right")])]}),makeQuery(id+"F31.opExtrude","SWEPT_FACE",FACE,{"disambiguationData":[OSD([sQuery(id+"F24.wireOp",EDGE,"E162.right")])]})]});
            extrude(context, id + "F44", {"entities" : qUnion([Q0]), "operationType" : NewBodyOperationType.ADD, "depth" : 1 * mm});
        }
        {
            var Q0;
            {var subQ0=sQuery(id+"F24.wireOp",EDGE,"E162.right");var subQ1=sQuery(id+"F24.wireOp",EDGE,"E161.right");var subQ2=sQuery(id+"F22.wireOp",EDGE,"E154.right");Q0=makeQuery(id+"F44.boolean.opBoolean","MERGE",FACE,{"derivedFrom":[makeQuery(id+"F31.boolean.opBoolean","MERGE",FACE,{"derivedFrom":[makeQuery(id+"F23.opExtrude","CAP_FACE",FACE,{"disambiguationData":[OSD([sQuery(id+"F22.wireOp",EDGE,"E153.bottom"),sQuery(id+"F22.wireOp",EDGE,"E153.top"),sQuery(id+"F22.wireOp",EDGE,"E153.left"),sQuery(id+"F22.wireOp",EDGE,"E153.right")])],"isStart":false}),makeQuery(id+"F23.opExtrude","CAP_FACE",FACE,{"disambiguationData":[OSD([sQuery(id+"F22.wireOp",EDGE,"E154.bottom"),sQuery(id+"F22.wireOp",EDGE,"E154.top"),sQuery(id+"F22.wireOp",EDGE,"E154.left"),subQ2])],"isStart":false}),makeQuery(id+"F31.opExtrude","CAP_FACE",FACE,{"disambiguationData":[OSD([sQuery(id+"F24.wireOp",EDGE,"E161.bottom"),sQuery(id+"F24.wireOp",EDGE,"E161.top"),sQuery(id+"F24.wireOp",EDGE,"E161.left"),subQ1,sQuery(id+"F24.wireOp",EDGE,"E165")])],"isStart":false}),makeQuery(id+"F31.opExtrude","CAP_FACE",FACE,{"disambiguationData":[OSD([sQuery(id+"F24.wireOp",EDGE,"E162.bottom"),sQuery(id+"F24.wireOp",EDGE,"E162.top"),sQuery(id+"F24.wireOp",EDGE,"E162.left"),subQ0,sQuery(id+"F24.wireOp",EDGE,"E166")])],"isStart":false})]}),makeQuery(id+"F44.opExtrude","SWEPT_FACE",FACE,{"disambiguationData":[OSD([subQ2,subQ1,subQ0]),TDD([makeQuery(id+"F31.boolean.opBoolean","MERGE",EDGE,{"derivedFrom":[makeQuery(id+"F23.opExtrude","CAP_EDGE",EDGE,{"disambiguationData":[OSD([subQ2])],"isStart":false}),makeQuery(id+"F31.opExtrude","CAP_EDGE",EDGE,{"disambiguationData":[OSD([subQ1])],"isStart":false}),makeQuery(id+"F31.opExtrude","CAP_EDGE",EDGE,{"disambiguationData":[OSD([subQ0])],"isStart":false})]})])]})]});}
            var sketch = newSketch(context, id + "F45", { "sketchPlane" : qUnion([Q0])});
            skLineSegment(sketch, "E182.bottom", {"start": v(-11.98, -171.06) * mm, "end": v(-13.98, -171.06) * mm});
            skLineSegment(sketch, "E182.top", {"start": v(-11.98, -134.06) * mm, "end": v(-13.98, -134.06) * mm});
            skLineSegment(sketch, "E182.left", {"start": v(-11.98, -171.06) * mm, "end": v(-11.98, -134.06) * mm});
            skLineSegment(sketch, "E182.right", {"start": v(-13.98, -171.06) * mm, "end": v(-13.98, -134.06) * mm});
            skSolve(sketch);
        }
        {
            var Q0;
            Q0=qSketchRegion(id+"F45",true);
            extrude(context, id + "F46", {"entities" : qUnion([Q0]), "operationType" : NewBodyOperationType.ADD, "depth" : 4 * mm});
        }
        {
            var Q0;
            Q0=qSketchRegion(id+"F39",true);
            extrude(context, id + "F47", {"entities" : qUnion([Q0]), "operationType" : NewBodyOperationType.REMOVE, "endBound" : BoundingType.THROUGH_ALL, "oppositeDirection" : true, "depth" : 3 * mm});
        }
        {
            var Q0;
            Q0=qSketchRegion(id+"F42",true);
            extrude(context, id + "F48", {"entities" : qUnion([Q0]), "operationType" : NewBodyOperationType.ADD, "depth" : 3 * mm});
        }
        {
            var Q0;
            Q0=makeQuery(id+"F31.boolean.opBoolean","MERGE",FACE,{"derivedFrom":[makeQuery(id+"F23.opExtrude","SWEPT_FACE",FACE,{"disambiguationData":[OSD([sQuery(id+"F22.wireOp",EDGE,"E150.right")])]}),makeQuery(id+"F31.opExtrude","SWEPT_FACE",FACE,{"disambiguationData":[OSD([sQuery(id+"F24.wireOp",EDGE,"E155.right")])]}),makeQuery(id+"F31.opExtrude","SWEPT_FACE",FACE,{"disambiguationData":[OSD([sQuery(id+"F24.wireOp",EDGE,"E156.right")])]})]});
            var Q1;
            Q1=makeQuery(id+"F31.boolean.opBoolean","MERGE",FACE,{"derivedFrom":[makeQuery(id+"F23.opExtrude","SWEPT_FACE",FACE,{"disambiguationData":[OSD([sQuery(id+"F22.wireOp",EDGE,"E152.right")])]}),makeQuery(id+"F31.opExtrude","SWEPT_FACE",FACE,{"disambiguationData":[OSD([sQuery(id+"F24.wireOp",EDGE,"E159.right")])]}),makeQuery(id+"F31.opExtrude","SWEPT_FACE",FACE,{"disambiguationData":[OSD([sQuery(id+"F24.wireOp",EDGE,"E160.right")])]})]});
            extrude(context, id + "F49", {"entities" : qUnion([Q0, Q1]), "operationType" : NewBodyOperationType.ADD, "depth" : 5 * mm});
        }
        {
            var Q0;
            Q0=makeQuery(id+"F16.imprint","IMPRINT",FACE,{"disambiguationData":[TD([[makeQuery(id+"F16.imprint","IMPRINT",EDGE,{"derivedFrom":sQuery(id+"F16.wireOp",EDGE,"E36")}),-1.0]])]});
            var Q1;
            {var subQ0=sQuery(id+"F16.wireOp",EDGE,"E133.left");Q1=makeQuery(id+"F32.boolean.opBoolean","MERGE",FACE,{"derivedFrom":[makeQuery(id+"F17.opExtrude","CAP_FACE",FACE,{"disambiguationData":[OSD([sQuery(id+"F16.wireOp",EDGE,"55227c07-3752-4080-a22d-609154aa437d.0"),sQuery(id+"F16.wireOp",EDGE,"55227c07-3752-4080-a22d-609154aa437d.1"),sQuery(id+"F16.wireOp",EDGE,"55227c07-3752-4080-a22d-609154aa437d.2"),sQuery(id+"F16.wireOp",EDGE,"55227c07-3752-4080-a22d-609154aa437d.3"),sQuery(id+"F16.wireOp",EDGE,"E36"),sQuery(id+"F16.wireOp",EDGE,"E38"),sQuery(id+"F16.wireOp",EDGE,"E43.left"),sQuery(id+"F16.wireOp",EDGE,"E43.right"),sQuery(id+"F16.wireOp",EDGE,"E44.left"),sQuery(id+"F16.wireOp",EDGE,"E44.right"),sQuery(id+"F16.wireOp",EDGE,"E45.bottom"),sQuery(id+"F16.wireOp",EDGE,"E45.top"),sQuery(id+"F16.wireOp",EDGE,"E46.trimOffspring"),sQuery(id+"F16.wireOp",EDGE,"E47.trimOffspring"),sQuery(id+"F16.wireOp",EDGE,"E50.trimOffspring"),sQuery(id+"F16.wireOp",EDGE,"E51.trimOffspring"),sQuery(id+"F16.wireOp",EDGE,"E52.trimOffspring"),sQuery(id+"F16.wireOp",EDGE,"E53.trimOffspring"),sQuery(id+"F16.wireOp",EDGE,"E54.trimOffspring"),sQuery(id+"F16.wireOp",EDGE,"E55.trimOffspring"),sQuery(id+"F16.wireOp",EDGE,"E56.bottom"),sQuery(id+"F16.wireOp",EDGE,"E56.left"),sQuery(id+"F16.wireOp",EDGE,"E56.top"),sQuery(id+"F16.wireOp",EDGE,"E56.right"),sQuery(id+"F16.wireOp",EDGE,"E59"),sQuery(id+"F16.wireOp",EDGE,"E61"),sQuery(id+"F16.wireOp",EDGE,"E66.left"),sQuery(id+"F16.wireOp",EDGE,"E66.right"),sQuery(id+"F16.wireOp",EDGE,"E67.left"),sQuery(id+"F16.wireOp",EDGE,"E67.right"),sQuery(id+"F16.wireOp",EDGE,"E68.bottom"),sQuery(id+"F16.wireOp",EDGE,"E68.top"),sQuery(id+"F16.wireOp",EDGE,"E69.trimOffspring"),sQuery(id+"F16.wireOp",EDGE,"E70.trimOffspring"),sQuery(id+"F16.wireOp",EDGE,"E73.trimOffspring"),sQuery(id+"F16.wireOp",EDGE,"E74.trimOffspring"),sQuery(id+"F16.wireOp",EDGE,"E75.trimOffspring"),sQuery(id+"F16.wireOp",EDGE,"E77.trimOffspring"),sQuery(id+"F16.wireOp",EDGE,"E78.trimOffspring"),sQuery(id+"F16.wireOp",EDGE,"E80.trimOffspring"),sQuery(id+"F16.wireOp",EDGE,"E81.bottom"),sQuery(id+"F16.wireOp",EDGE,"E81.left"),sQuery(id+"F16.wireOp",EDGE,"E81.top"),sQuery(id+"F16.wireOp",EDGE,"E81.right"),sQuery(id+"F16.wireOp",EDGE,"E85"),sQuery(id+"F16.wireOp",EDGE,"E87"),sQuery(id+"F16.wireOp",EDGE,"E92.left"),sQuery(id+"F16.wireOp",EDGE,"E92.right"),sQuery(id+"F16.wireOp",EDGE,"E93.left"),sQuery(id+"F16.wireOp",EDGE,"E93.right"),sQuery(id+"F16.wireOp",EDGE,"E94.bottom"),sQuery(id+"F16.wireOp",EDGE,"E94.top"),sQuery(id+"F16.wireOp",EDGE,"E95.trimOffspring"),sQuery(id+"F16.wireOp",EDGE,"E96.trimOffspring"),sQuery(id+"F16.wireOp",EDGE,"E99.trimOffspring"),sQuery(id+"F16.wireOp",EDGE,"E100.trimOffspring"),sQuery(id+"F16.wireOp",EDGE,"E101.trimOffspring"),sQuery(id+"F16.wireOp",EDGE,"E103.trimOffspring"),sQuery(id+"F16.wireOp",EDGE,"E104.trimOffspring"),sQuery(id+"F16.wireOp",EDGE,"E106.trimOffspring"),sQuery(id+"F16.wireOp",EDGE,"E107.bottom"),sQuery(id+"F16.wireOp",EDGE,"E107.left"),sQuery(id+"F16.wireOp",EDGE,"E107.top"),sQuery(id+"F16.wireOp",EDGE,"E107.right"),sQuery(id+"F16.wireOp",EDGE,"E111"),sQuery(id+"F16.wireOp",EDGE,"E113"),sQuery(id+"F16.wireOp",EDGE,"E118.left"),sQuery(id+"F16.wireOp",EDGE,"E118.right"),sQuery(id+"F16.wireOp",EDGE,"E119.left"),sQuery(id+"F16.wireOp",EDGE,"E119.right"),sQuery(id+"F16.wireOp",EDGE,"E120.bottom"),sQuery(id+"F16.wireOp",EDGE,"E120.top"),sQuery(id+"F16.wireOp",EDGE,"E121.trimOffspring"),sQuery(id+"F16.wireOp",EDGE,"E122.trimOffspring"),sQuery(id+"F16.wireOp",EDGE,"E125.trimOffspring"),sQuery(id+"F16.wireOp",EDGE,"E126.trimOffspring"),sQuery(id+"F16.wireOp",EDGE,"E127.trimOffspring"),sQuery(id+"F16.wireOp",EDGE,"E129.trimOffspring"),sQuery(id+"F16.wireOp",EDGE,"E130.trimOffspring"),sQuery(id+"F16.wireOp",EDGE,"E132.trimOffspring"),sQuery(id+"F16.wireOp",EDGE,"E133.bottom"),sQuery(id+"F16.wireOp",EDGE,"E133.top"),subQ0,sQuery(id+"F16.wireOp",EDGE,"E133.right")])],"isStart":true}),makeQuery(id+"F32.opExtrude","SWEPT_FACE",FACE,{"disambiguationData":[OSD([subQ0]),TDD([makeQuery(id+"F17.opExtrude","CAP_EDGE",EDGE,{"disambiguationData":[OSD([subQ0])],"isStart":true})])]})]});}
            extrude(context, id + "F50", {"entities" : qUnion([Q0, Q1]), "operationType" : NewBodyOperationType.ADD, "oppositeDirection" : true, "depth" : 1 * mm});
        }
        {
            var Q0;
            Q0=makeQuery(id+"F19.opExtrude","CAP_FACE",FACE,{"disambiguationData":[OSD([sQuery(id+"F18.wireOp",EDGE,"E134.bottom"),sQuery(id+"F18.wireOp",EDGE,"E134.top"),sQuery(id+"F18.wireOp",EDGE,"E134.left"),sQuery(id+"F18.wireOp",EDGE,"E134.right"),sQuery(id+"F18.wireOp",EDGE,"E135.bottom"),sQuery(id+"F18.wireOp",EDGE,"E135.top"),sQuery(id+"F18.wireOp",EDGE,"E135.left"),sQuery(id+"F18.wireOp",EDGE,"E135.right"),sQuery(id+"F18.wireOp",EDGE,"E138.bottom"),sQuery(id+"F18.wireOp",EDGE,"E138.top"),sQuery(id+"F18.wireOp",EDGE,"E138.left"),sQuery(id+"F18.wireOp",EDGE,"E138.right"),sQuery(id+"F18.wireOp",EDGE,"E141.bottom"),sQuery(id+"F18.wireOp",EDGE,"E141.top"),sQuery(id+"F18.wireOp",EDGE,"E141.left"),sQuery(id+"F18.wireOp",EDGE,"E141.right"),sQuery(id+"F18.wireOp",EDGE,"E144.bottom"),sQuery(id+"F18.wireOp",EDGE,"E144.top"),sQuery(id+"F18.wireOp",EDGE,"E144.left"),sQuery(id+"F18.wireOp",EDGE,"E144.right")])],"isStart":true});
            extrude(context, id + "F51", {"entities" : qUnion([Q0]), "operationType" : NewBodyOperationType.ADD, "depth" : 1 * mm});
        }
        {
            var Q0;
            {var subQ0=sQuery(id+"F24.wireOp",EDGE,"E162.right");var subQ1=sQuery(id+"F24.wireOp",EDGE,"E161.right");var subQ2=sQuery(id+"F22.wireOp",EDGE,"E154.right");Q0=makeQuery(id+"F44.opExtrude","SWEPT_FACE",FACE,{"disambiguationData":[OSD([subQ2,subQ1,subQ0]),TDD([makeQuery(id+"F31.boolean.opBoolean","MERGE",EDGE,{"derivedFrom":[makeQuery(id+"F23.opExtrude","CAP_EDGE",EDGE,{"disambiguationData":[OSD([subQ2])],"isStart":true}),makeQuery(id+"F31.opExtrude","CAP_EDGE",EDGE,{"disambiguationData":[OSD([subQ1])],"isStart":true}),makeQuery(id+"F31.opExtrude","CAP_EDGE",EDGE,{"disambiguationData":[OSD([subQ0])],"isStart":true})]})])]});}
            extrude(context, id + "F52", {"entities" : qUnion([Q0]), "operationType" : NewBodyOperationType.ADD, "depth" : 2 * mm});
        }
        {
            var Q0;
            {var subQ1=sQuery(id+"F9.wireOp",EDGE,"E19.bottom");var subQ2=sQuery(id+"F9.wireOp",EDGE,"E18.right");var subQ3=sQuery(id+"F9.wireOp",EDGE,"E18.top");var subQ4=sQuery(id+"F9.wireOp",EDGE,"E18.bottom");var subQ5=sQuery(id+"F9.wireOp",EDGE,"E17.right");var subQ6=sQuery(id+"F9.wireOp",EDGE,"E17.top");var subQ7=sQuery(id+"F9.wireOp",EDGE,"E17.bottom");var subQ8=sQuery(id+"F9.wireOp",EDGE,"E16.right");var subQ9=sQuery(id+"F9.wireOp",EDGE,"E16.left");var subQ10=sQuery(id+"F9.wireOp",EDGE,"E15.right");var subQ11=sQuery(id+"F9.wireOp",EDGE,"E15.left");var subQ12=sQuery(id+"F9.wireOp",EDGE,"E15.top");var subQ13=makeQuery(id+"F10.opExtrude","CAP_FACE",FACE,{"disambiguationData":[OSD([subQ12,subQ11,subQ10,subQ9,subQ8,subQ7,subQ6,subQ5,subQ4,subQ3,subQ2,subQ1])],"isStart":false});Q0=makeQuery(id+"F30.opFillet","MERGE",FACE,{"derivedFrom":[makeQuery(id+"F10.boolean.opBoolean","SPLIT",FACE,{"disambiguationData":[TD([makeQuery(id+"F10.opExtrude","SWEPT_FACE",FACE,{"disambiguationData":[OSD([subQ12])]})])],"derivedFrom":subQ13}),makeQuery(id+"F10.boolean.opBoolean","SPLIT",FACE,{"disambiguationData":[TD([makeQuery(id+"F10.opExtrude","SWEPT_FACE",FACE,{"disambiguationData":[OSD([subQ1])]})])],"derivedFrom":subQ13}),makeQuery(id+"F10.boolean.opBoolean","SPLIT",FACE,{"disambiguationData":[TD([makeQuery(id+"F10.opExtrude","SWEPT_FACE",FACE,{"disambiguationData":[OSD([subQ5])]})])],"derivedFrom":subQ13}),makeQuery(id+"F10.boolean.opBoolean","SPLIT",FACE,{"disambiguationData":[TD([makeQuery(id+"F10.opExtrude","SWEPT_FACE",FACE,{"disambiguationData":[OSD([subQ2])]})])],"derivedFrom":subQ13})]});}
            extrude(context, id + "F53", {"entities" : qUnion([Q0]), "operationType" : NewBodyOperationType.ADD, "depth" : 0.05 * mm});
        }
        {
            var Q0;
            Q0=makeQuery(id+"F19.opExtrude","CAP_FACE",FACE,{"disambiguationData":[OSD([sQuery(id+"F18.wireOp",EDGE,"E134.bottom"),sQuery(id+"F18.wireOp",EDGE,"E134.top"),sQuery(id+"F18.wireOp",EDGE,"E134.left"),sQuery(id+"F18.wireOp",EDGE,"E134.right"),sQuery(id+"F18.wireOp",EDGE,"E135.bottom"),sQuery(id+"F18.wireOp",EDGE,"E135.top"),sQuery(id+"F18.wireOp",EDGE,"E135.left"),sQuery(id+"F18.wireOp",EDGE,"E135.right"),sQuery(id+"F18.wireOp",EDGE,"E138.bottom"),sQuery(id+"F18.wireOp",EDGE,"E138.top"),sQuery(id+"F18.wireOp",EDGE,"E138.left"),sQuery(id+"F18.wireOp",EDGE,"E138.right"),sQuery(id+"F18.wireOp",EDGE,"E141.bottom"),sQuery(id+"F18.wireOp",EDGE,"E141.top"),sQuery(id+"F18.wireOp",EDGE,"E141.left"),sQuery(id+"F18.wireOp",EDGE,"E141.right"),sQuery(id+"F18.wireOp",EDGE,"E144.bottom"),sQuery(id+"F18.wireOp",EDGE,"E144.top"),sQuery(id+"F18.wireOp",EDGE,"E144.left"),sQuery(id+"F18.wireOp",EDGE,"E144.right")])],"isStart":false});
            var sketch = newSketch(context, id + "F54", { "sketchPlane" : qUnion([Q0])});
            skLineSegment(sketch, "E183.bottom", {"start": v(22.06, -144.26) * mm, "end": v(42.46, -144.26) * mm});
            skLineSegment(sketch, "E183.top", {"start": v(22.06, -141.26) * mm, "end": v(42.46, -141.26) * mm});
            skLineSegment(sketch, "E183.left", {"start": v(22.06, -144.26) * mm, "end": v(22.06, -141.26) * mm});
            skLineSegment(sketch, "E183.right", {"start": v(42.46, -144.26) * mm, "end": v(42.46, -141.26) * mm});
            skLineSegment(sketch, "E184.bottom", {"start": v(22.06, -164.66) * mm, "end": v(42.46, -164.66) * mm});
            skLineSegment(sketch, "E184.top", {"start": v(22.06, -167.66) * mm, "end": v(42.46, -167.66) * mm});
            skLineSegment(sketch, "E184.left", {"start": v(22.06, -164.66) * mm, "end": v(22.06, -167.66) * mm});
            skLineSegment(sketch, "E184.right", {"start": v(42.46, -164.66) * mm, "end": v(42.46, -167.66) * mm});
            skLineSegment(sketch, "E185.bottom", {"start": v(22.06, -141.26) * mm, "end": v(19.06, -141.26) * mm});
            skLineSegment(sketch, "E185.top", {"start": v(22.06, -167.66) * mm, "end": v(19.06, -167.66) * mm});
            skLineSegment(sketch, "E185.left", {"start": v(22.06, -141.26) * mm, "end": v(22.06, -167.66) * mm});
            skLineSegment(sketch, "E185.right", {"start": v(19.06, -141.26) * mm, "end": v(19.06, -167.66) * mm});
            skLineSegment(sketch, "E186.bottom", {"start": v(42.46, -141.26) * mm, "end": v(45.46, -141.26) * mm});
            skLineSegment(sketch, "E186.top", {"start": v(42.46, -167.66) * mm, "end": v(45.46, -167.66) * mm});
            skLineSegment(sketch, "E186.left", {"start": v(42.46, -141.26) * mm, "end": v(42.46, -167.66) * mm});
            skLineSegment(sketch, "E186.right", {"start": v(45.46, -141.26) * mm, "end": v(45.46, -167.66) * mm});
            skLineSegment(sketch, "E187.bottom", {"start": v(52.16, -144.36) * mm, "end": v(72.36, -144.36) * mm});
            skLineSegment(sketch, "E187.top", {"start": v(52.16, -141.26) * mm, "end": v(72.36, -141.26) * mm});
            skLineSegment(sketch, "E187.left", {"start": v(52.16, -144.36) * mm, "end": v(52.16, -141.26) * mm});
            skLineSegment(sketch, "E187.right", {"start": v(72.36, -144.36) * mm, "end": v(72.36, -141.26) * mm});
            skLineSegment(sketch, "E188.bottom", {"start": v(52.16, -141.26) * mm, "end": v(49.16, -141.26) * mm});
            skLineSegment(sketch, "E188.top", {"start": v(52.16, -167.66) * mm, "end": v(49.16, -167.66) * mm});
            skLineSegment(sketch, "E188.left", {"start": v(52.16, -141.26) * mm, "end": v(52.16, -167.66) * mm});
            skLineSegment(sketch, "E188.right", {"start": v(49.16, -141.26) * mm, "end": v(49.16, -167.66) * mm});
            skLineSegment(sketch, "E189.bottom", {"start": v(52.16, -167.66) * mm, "end": v(72.36, -167.66) * mm});
            skLineSegment(sketch, "E189.top", {"start": v(52.16, -164.56) * mm, "end": v(72.36, -164.56) * mm});
            skLineSegment(sketch, "E189.left", {"start": v(52.16, -167.66) * mm, "end": v(52.16, -164.56) * mm});
            skLineSegment(sketch, "E189.right", {"start": v(72.36, -167.66) * mm, "end": v(72.36, -164.56) * mm});
            skLineSegment(sketch, "E190.bottom", {"start": v(72.36, -167.66) * mm, "end": v(75.36, -167.66) * mm});
            skLineSegment(sketch, "E190.top", {"start": v(72.36, -141.26) * mm, "end": v(75.36, -141.26) * mm});
            skLineSegment(sketch, "E190.left", {"start": v(72.36, -167.66) * mm, "end": v(72.36, -141.26) * mm});
            skLineSegment(sketch, "E190.right", {"start": v(75.36, -167.66) * mm, "end": v(75.36, -141.26) * mm});
            skLineSegment(sketch, "E191.bottom", {"start": v(82.16, -144.36) * mm, "end": v(102.36, -144.36) * mm});
            skLineSegment(sketch, "E191.top", {"start": v(82.16, -141.26) * mm, "end": v(102.36, -141.26) * mm});
            skLineSegment(sketch, "E191.left", {"start": v(82.16, -144.36) * mm, "end": v(82.16, -141.26) * mm});
            skLineSegment(sketch, "E191.right", {"start": v(102.36, -144.36) * mm, "end": v(102.36, -141.26) * mm});
            skLineSegment(sketch, "E192.bottom", {"start": v(82.16, -141.26) * mm, "end": v(79.16, -141.26) * mm});
            skLineSegment(sketch, "E192.top", {"start": v(82.16, -167.66) * mm, "end": v(79.16, -167.66) * mm});
            skLineSegment(sketch, "E192.left", {"start": v(82.16, -141.26) * mm, "end": v(82.16, -167.66) * mm});
            skLineSegment(sketch, "E192.right", {"start": v(79.16, -141.26) * mm, "end": v(79.16, -167.66) * mm});
            skLineSegment(sketch, "E193.bottom", {"start": v(82.16, -167.66) * mm, "end": v(102.36, -167.66) * mm});
            skLineSegment(sketch, "E193.top", {"start": v(82.16, -164.56) * mm, "end": v(102.36, -164.56) * mm});
            skLineSegment(sketch, "E193.left", {"start": v(82.16, -167.66) * mm, "end": v(82.16, -164.56) * mm});
            skLineSegment(sketch, "E193.right", {"start": v(102.36, -167.66) * mm, "end": v(102.36, -164.56) * mm});
            skLineSegment(sketch, "E194.bottom", {"start": v(102.36, -141.26) * mm, "end": v(105.36, -141.26) * mm});
            skLineSegment(sketch, "E194.top", {"start": v(102.36, -167.66) * mm, "end": v(105.36, -167.66) * mm});
            skLineSegment(sketch, "E194.left", {"start": v(102.36, -141.26) * mm, "end": v(102.36, -167.66) * mm});
            skLineSegment(sketch, "E194.right", {"start": v(105.36, -141.26) * mm, "end": v(105.36, -167.66) * mm});
            skLineSegment(sketch, "E195.bottom", {"start": v(112.16, -144.36) * mm, "end": v(132.36, -144.36) * mm});
            skLineSegment(sketch, "E195.top", {"start": v(112.16, -141.26) * mm, "end": v(132.36, -141.26) * mm});
            skLineSegment(sketch, "E195.left", {"start": v(112.16, -144.36) * mm, "end": v(112.16, -141.26) * mm});
            skLineSegment(sketch, "E195.right", {"start": v(132.36, -144.36) * mm, "end": v(132.36, -141.26) * mm});
            skLineSegment(sketch, "E196.bottom", {"start": v(112.16, -141.26) * mm, "end": v(109.16, -141.26) * mm});
            skLineSegment(sketch, "E196.top", {"start": v(112.16, -167.66) * mm, "end": v(109.16, -167.66) * mm});
            skLineSegment(sketch, "E196.left", {"start": v(112.16, -141.26) * mm, "end": v(112.16, -167.66) * mm});
            skLineSegment(sketch, "E196.right", {"start": v(109.16, -141.26) * mm, "end": v(109.16, -167.66) * mm});
            skLineSegment(sketch, "E197.bottom", {"start": v(112.16, -167.66) * mm, "end": v(132.36, -167.66) * mm});
            skLineSegment(sketch, "E197.top", {"start": v(112.16, -164.56) * mm, "end": v(132.36, -164.56) * mm});
            skLineSegment(sketch, "E197.left", {"start": v(112.16, -167.66) * mm, "end": v(112.16, -164.56) * mm});
            skLineSegment(sketch, "E197.right", {"start": v(132.36, -167.66) * mm, "end": v(132.36, -164.56) * mm});
            skLineSegment(sketch, "E198.bottom", {"start": v(132.36, -141.26) * mm, "end": v(135.36, -141.26) * mm});
            skLineSegment(sketch, "E198.top", {"start": v(132.36, -167.66) * mm, "end": v(135.36, -167.66) * mm});
            skLineSegment(sketch, "E198.left", {"start": v(132.36, -141.26) * mm, "end": v(132.36, -167.66) * mm});
            skLineSegment(sketch, "E198.right", {"start": v(135.36, -141.26) * mm, "end": v(135.36, -167.66) * mm});
            skSolve(sketch);
        }
        {
            var Q0;
            Q0=qSketchRegion(id+"F54",true);
            extrude(context, id + "F55", {"entities" : qUnion([Q0]), "operationType" : NewBodyOperationType.ADD, "depth" : 0.5 * mm});
        }
        {
            var Q0;
            Q0=makeQuery(id+"F55.opExtrude","CAP_FACE",FACE,{"disambiguationData":[OSD([sQuery(id+"F54.wireOp",EDGE,"E183.bottom"),sQuery(id+"F54.wireOp",EDGE,"E183.top"),sQuery(id+"F54.wireOp",EDGE,"E184.bottom"),sQuery(id+"F54.wireOp",EDGE,"E184.top"),sQuery(id+"F54.wireOp",EDGE,"E185.bottom"),sQuery(id+"F54.wireOp",EDGE,"E185.top"),sQuery(id+"F54.wireOp",EDGE,"E185.left"),sQuery(id+"F54.wireOp",EDGE,"E185.right"),sQuery(id+"F54.wireOp",EDGE,"E186.bottom"),sQuery(id+"F54.wireOp",EDGE,"E186.top"),sQuery(id+"F54.wireOp",EDGE,"E186.left"),sQuery(id+"F54.wireOp",EDGE,"E186.right")])],"isStart":false});
            var sketch = newSketch(context, id + "F56", { "sketchPlane" : qUnion([Q0])});
            skLineSegment(sketch, "E199.bottom", {"start": v(22.06, -144.26) * mm, "end": v(42.46, -144.26) * mm});
            skLineSegment(sketch, "E199.top", {"start": v(22.06, -142.76) * mm, "end": v(42.46, -142.76) * mm});
            skLineSegment(sketch, "E199.left", {"start": v(22.06, -144.26) * mm, "end": v(22.06, -142.76) * mm});
            skLineSegment(sketch, "E199.right", {"start": v(42.46, -144.26) * mm, "end": v(42.46, -142.76) * mm});
            skLineSegment(sketch, "E200.bottom", {"start": v(22.06, -164.66) * mm, "end": v(42.46, -164.66) * mm});
            skLineSegment(sketch, "E200.top", {"start": v(22.06, -166.16) * mm, "end": v(42.46, -166.16) * mm});
            skLineSegment(sketch, "E200.left", {"start": v(22.06, -164.66) * mm, "end": v(22.06, -166.16) * mm});
            skLineSegment(sketch, "E200.right", {"start": v(42.46, -164.66) * mm, "end": v(42.46, -166.16) * mm});
            skLineSegment(sketch, "E201.bottom", {"start": v(22.06, -166.16) * mm, "end": v(20.56, -166.16) * mm});
            skLineSegment(sketch, "E201.top", {"start": v(22.06, -142.76) * mm, "end": v(20.56, -142.76) * mm});
            skLineSegment(sketch, "E201.left", {"start": v(22.06, -166.16) * mm, "end": v(22.06, -142.76) * mm});
            skLineSegment(sketch, "E201.right", {"start": v(20.56, -166.16) * mm, "end": v(20.56, -142.76) * mm});
            skLineSegment(sketch, "E202.bottom", {"start": v(42.46, -166.16) * mm, "end": v(43.96, -166.16) * mm});
            skLineSegment(sketch, "E202.top", {"start": v(42.46, -142.76) * mm, "end": v(43.96, -142.76) * mm});
            skLineSegment(sketch, "E202.left", {"start": v(42.46, -166.16) * mm, "end": v(42.46, -142.76) * mm});
            skLineSegment(sketch, "E202.right", {"start": v(43.96, -166.16) * mm, "end": v(43.96, -142.76) * mm});
            skLineSegment(sketch, "E203.bottom", {"start": v(50.66, -142.86) * mm, "end": v(52.16, -142.86) * mm});
            skLineSegment(sketch, "E203.top", {"start": v(50.66, -166.06) * mm, "end": v(52.16, -166.06) * mm});
            skLineSegment(sketch, "E203.left", {"start": v(50.66, -142.86) * mm, "end": v(50.66, -166.06) * mm});
            skLineSegment(sketch, "E203.right", {"start": v(52.16, -142.86) * mm, "end": v(52.16, -166.06) * mm});
            skLineSegment(sketch, "E204.bottom", {"start": v(72.36, -142.86) * mm, "end": v(73.86, -142.86) * mm});
            skLineSegment(sketch, "E204.top", {"start": v(72.36, -166.06) * mm, "end": v(73.86, -166.06) * mm});
            skLineSegment(sketch, "E204.left", {"start": v(72.36, -142.86) * mm, "end": v(72.36, -166.06) * mm});
            skLineSegment(sketch, "E204.right", {"start": v(73.86, -142.86) * mm, "end": v(73.86, -166.06) * mm});
            skLineSegment(sketch, "E205.bottom", {"start": v(52.16, -142.86) * mm, "end": v(72.36, -142.86) * mm});
            skLineSegment(sketch, "E205.top", {"start": v(52.16, -144.36) * mm, "end": v(72.36, -144.36) * mm});
            skLineSegment(sketch, "E205.left", {"start": v(52.16, -142.86) * mm, "end": v(52.16, -144.36) * mm});
            skLineSegment(sketch, "E205.right", {"start": v(72.36, -142.86) * mm, "end": v(72.36, -144.36) * mm});
            skLineSegment(sketch, "E206.bottom", {"start": v(52.16, -166.06) * mm, "end": v(72.36, -166.06) * mm});
            skLineSegment(sketch, "E206.top", {"start": v(52.16, -164.56) * mm, "end": v(72.36, -164.56) * mm});
            skLineSegment(sketch, "E206.left", {"start": v(52.16, -166.06) * mm, "end": v(52.16, -164.56) * mm});
            skLineSegment(sketch, "E206.right", {"start": v(72.36, -166.06) * mm, "end": v(72.36, -164.56) * mm});
            skLineSegment(sketch, "E207.bottom", {"start": v(80.66, -142.86) * mm, "end": v(82.16, -142.86) * mm});
            skLineSegment(sketch, "E207.top", {"start": v(80.66, -166.06) * mm, "end": v(82.16, -166.06) * mm});
            skLineSegment(sketch, "E207.left", {"start": v(80.66, -142.86) * mm, "end": v(80.66, -166.06) * mm});
            skLineSegment(sketch, "E207.right", {"start": v(82.16, -142.86) * mm, "end": v(82.16, -166.06) * mm});
            skLineSegment(sketch, "E208.bottom", {"start": v(82.16, -142.86) * mm, "end": v(102.36, -142.86) * mm});
            skLineSegment(sketch, "E208.top", {"start": v(82.16, -144.36) * mm, "end": v(102.36, -144.36) * mm});
            skLineSegment(sketch, "E208.left", {"start": v(82.16, -142.86) * mm, "end": v(82.16, -144.36) * mm});
            skLineSegment(sketch, "E208.right", {"start": v(102.36, -142.86) * mm, "end": v(102.36, -144.36) * mm});
            skLineSegment(sketch, "E209.bottom", {"start": v(82.16, -166.06) * mm, "end": v(102.36, -166.06) * mm});
            skLineSegment(sketch, "E209.top", {"start": v(82.16, -164.56) * mm, "end": v(102.36, -164.56) * mm});
            skLineSegment(sketch, "E209.left", {"start": v(82.16, -166.06) * mm, "end": v(82.16, -164.56) * mm});
            skLineSegment(sketch, "E209.right", {"start": v(102.36, -166.06) * mm, "end": v(102.36, -164.56) * mm});
            skLineSegment(sketch, "E210.bottom", {"start": v(102.36, -166.06) * mm, "end": v(103.86, -166.06) * mm});
            skLineSegment(sketch, "E210.top", {"start": v(102.36, -142.86) * mm, "end": v(103.86, -142.86) * mm});
            skLineSegment(sketch, "E210.left", {"start": v(102.36, -166.06) * mm, "end": v(102.36, -142.86) * mm});
            skLineSegment(sketch, "E210.right", {"start": v(103.86, -166.06) * mm, "end": v(103.86, -142.86) * mm});
            skLineSegment(sketch, "E211.bottom", {"start": v(110.76, -142.86) * mm, "end": v(112.26, -142.86) * mm});
            skLineSegment(sketch, "E211.top", {"start": v(110.76, -166.06) * mm, "end": v(112.26, -166.06) * mm});
            skLineSegment(sketch, "E211.left", {"start": v(110.76, -142.86) * mm, "end": v(110.76, -166.06) * mm});
            skLineSegment(sketch, "E211.right", {"start": v(112.26, -142.86) * mm, "end": v(112.26, -166.06) * mm});
            skLineSegment(sketch, "E212.bottom", {"start": v(112.26, -142.86) * mm, "end": v(132.46, -142.86) * mm});
            skLineSegment(sketch, "E212.top", {"start": v(112.26, -144.36) * mm, "end": v(132.46, -144.36) * mm});
            skLineSegment(sketch, "E212.left", {"start": v(112.26, -142.86) * mm, "end": v(112.26, -144.36) * mm});
            skLineSegment(sketch, "E212.right", {"start": v(132.46, -142.86) * mm, "end": v(132.46, -144.36) * mm});
            skLineSegment(sketch, "E213.bottom", {"start": v(112.26, -166.06) * mm, "end": v(132.46, -166.06) * mm});
            skLineSegment(sketch, "E213.top", {"start": v(112.26, -164.56) * mm, "end": v(132.46, -164.56) * mm});
            skLineSegment(sketch, "E213.left", {"start": v(112.26, -166.06) * mm, "end": v(112.26, -164.56) * mm});
            skLineSegment(sketch, "E213.right", {"start": v(132.46, -166.06) * mm, "end": v(132.46, -164.56) * mm});
            skLineSegment(sketch, "E214.bottom", {"start": v(132.46, -166.06) * mm, "end": v(133.96, -166.06) * mm});
            skLineSegment(sketch, "E214.top", {"start": v(132.46, -142.86) * mm, "end": v(133.96, -142.86) * mm});
            skLineSegment(sketch, "E214.left", {"start": v(132.46, -166.06) * mm, "end": v(132.46, -142.86) * mm});
            skLineSegment(sketch, "E214.right", {"start": v(133.96, -166.06) * mm, "end": v(133.96, -142.86) * mm});
            skSolve(sketch);
        }
        {
            var Q0;
            Q0=qSketchRegion(id+"F56",true);
            extrude(context, id + "F57", {"entities" : qUnion([Q0]), "operationType" : NewBodyOperationType.ADD, "depth" : 1 * mm});
        }
        {
            var Q0;
            Q0=makeQuery(id+"F55.opExtrude","SWEPT_EDGE",EDGE,{"disambiguationData":[OSD([sQuery(id+"F54.wireOp",EDGE,"E185.bottom"),sQuery(id+"F54.wireOp",EDGE,"E185.right")])]});
            var Q1;
            Q1=makeQuery(id+"F57.opExtrude","SWEPT_EDGE",EDGE,{"disambiguationData":[OSD([sQuery(id+"F56.wireOp",EDGE,"E201.top"),sQuery(id+"F56.wireOp",EDGE,"E201.right")])]});
            var Q2;
            Q2=makeQuery(id+"F55.opExtrude","SWEPT_EDGE",EDGE,{"disambiguationData":[OSD([sQuery(id+"F54.wireOp",EDGE,"E185.top"),sQuery(id+"F54.wireOp",EDGE,"E185.right")])]});
            var Q3;
            Q3=makeQuery(id+"F57.opExtrude","SWEPT_EDGE",EDGE,{"disambiguationData":[OSD([sQuery(id+"F56.wireOp",EDGE,"E201.bottom"),sQuery(id+"F56.wireOp",EDGE,"E201.right")])]});
            var Q4;
            Q4=makeQuery(id+"F57.opExtrude","SWEPT_EDGE",EDGE,{"disambiguationData":[OSD([sQuery(id+"F56.wireOp",EDGE,"E202.bottom"),sQuery(id+"F56.wireOp",EDGE,"E202.right")])]});
            var Q5;
            Q5=makeQuery(id+"F55.opExtrude","SWEPT_EDGE",EDGE,{"disambiguationData":[OSD([sQuery(id+"F54.wireOp",EDGE,"E186.top"),sQuery(id+"F54.wireOp",EDGE,"E186.right")])]});
            var Q6;
            Q6=makeQuery(id+"F57.opExtrude","SWEPT_EDGE",EDGE,{"disambiguationData":[OSD([sQuery(id+"F56.wireOp",EDGE,"E202.top"),sQuery(id+"F56.wireOp",EDGE,"E202.right")])]});
            var Q7;
            Q7=makeQuery(id+"F55.opExtrude","SWEPT_EDGE",EDGE,{"disambiguationData":[OSD([sQuery(id+"F54.wireOp",EDGE,"E186.bottom"),sQuery(id+"F54.wireOp",EDGE,"E186.right")])]});
            var Q8;
            Q8=makeQuery(id+"F55.opExtrude","SWEPT_EDGE",EDGE,{"disambiguationData":[OSD([sQuery(id+"F54.wireOp",EDGE,"E188.bottom"),sQuery(id+"F54.wireOp",EDGE,"E188.right")])]});
            var Q9;
            Q9=makeQuery(id+"F57.opExtrude","SWEPT_EDGE",EDGE,{"disambiguationData":[OSD([sQuery(id+"F56.wireOp",EDGE,"E203.bottom"),sQuery(id+"F56.wireOp",EDGE,"E203.left")])]});
            var Q10;
            Q10=makeQuery(id+"F57.opExtrude","SWEPT_EDGE",EDGE,{"disambiguationData":[OSD([sQuery(id+"F56.wireOp",EDGE,"E203.top"),sQuery(id+"F56.wireOp",EDGE,"E203.left")])]});
            var Q11;
            Q11=makeQuery(id+"F55.opExtrude","SWEPT_EDGE",EDGE,{"disambiguationData":[OSD([sQuery(id+"F54.wireOp",EDGE,"E188.top"),sQuery(id+"F54.wireOp",EDGE,"E188.right")])]});
            var Q12;
            Q12=makeQuery(id+"F57.opExtrude","SWEPT_EDGE",EDGE,{"disambiguationData":[OSD([sQuery(id+"F56.wireOp",EDGE,"E204.top"),sQuery(id+"F56.wireOp",EDGE,"E204.right")])]});
            var Q13;
            Q13=makeQuery(id+"F55.opExtrude","SWEPT_EDGE",EDGE,{"disambiguationData":[OSD([sQuery(id+"F54.wireOp",EDGE,"E190.bottom"),sQuery(id+"F54.wireOp",EDGE,"E190.right")])]});
            var Q14;
            Q14=makeQuery(id+"F57.opExtrude","SWEPT_EDGE",EDGE,{"disambiguationData":[OSD([sQuery(id+"F56.wireOp",EDGE,"E204.bottom"),sQuery(id+"F56.wireOp",EDGE,"E204.right")])]});
            var Q15;
            Q15=makeQuery(id+"F55.opExtrude","SWEPT_EDGE",EDGE,{"disambiguationData":[OSD([sQuery(id+"F54.wireOp",EDGE,"E190.top"),sQuery(id+"F54.wireOp",EDGE,"E190.right")])]});
            var Q16;
            Q16=makeQuery(id+"F55.opExtrude","SWEPT_EDGE",EDGE,{"disambiguationData":[OSD([sQuery(id+"F54.wireOp",EDGE,"E192.bottom"),sQuery(id+"F54.wireOp",EDGE,"E192.right")])]});
            var Q17;
            Q17=makeQuery(id+"F57.opExtrude","SWEPT_EDGE",EDGE,{"disambiguationData":[OSD([sQuery(id+"F56.wireOp",EDGE,"E207.bottom"),sQuery(id+"F56.wireOp",EDGE,"E207.left")])]});
            var Q18;
            Q18=makeQuery(id+"F55.opExtrude","SWEPT_EDGE",EDGE,{"disambiguationData":[OSD([sQuery(id+"F54.wireOp",EDGE,"E192.top"),sQuery(id+"F54.wireOp",EDGE,"E192.right")])]});
            var Q19;
            Q19=makeQuery(id+"F57.opExtrude","SWEPT_EDGE",EDGE,{"disambiguationData":[OSD([sQuery(id+"F56.wireOp",EDGE,"E207.top"),sQuery(id+"F56.wireOp",EDGE,"E207.left")])]});
            var Q20;
            Q20=makeQuery(id+"F57.opExtrude","SWEPT_EDGE",EDGE,{"disambiguationData":[OSD([sQuery(id+"F56.wireOp",EDGE,"E210.bottom"),sQuery(id+"F56.wireOp",EDGE,"E210.right")])]});
            var Q21;
            Q21=makeQuery(id+"F55.opExtrude","SWEPT_EDGE",EDGE,{"disambiguationData":[OSD([sQuery(id+"F54.wireOp",EDGE,"E194.top"),sQuery(id+"F54.wireOp",EDGE,"E194.right")])]});
            var Q22;
            Q22=makeQuery(id+"F57.opExtrude","SWEPT_EDGE",EDGE,{"disambiguationData":[OSD([sQuery(id+"F56.wireOp",EDGE,"E210.top"),sQuery(id+"F56.wireOp",EDGE,"E210.right")])]});
            var Q23;
            Q23=makeQuery(id+"F55.opExtrude","SWEPT_EDGE",EDGE,{"disambiguationData":[OSD([sQuery(id+"F54.wireOp",EDGE,"E194.bottom"),sQuery(id+"F54.wireOp",EDGE,"E194.right")])]});
            var Q24;
            Q24=makeQuery(id+"F55.opExtrude","SWEPT_EDGE",EDGE,{"disambiguationData":[OSD([sQuery(id+"F54.wireOp",EDGE,"E196.bottom"),sQuery(id+"F54.wireOp",EDGE,"E196.right")])]});
            var Q25;
            Q25=makeQuery(id+"F57.opExtrude","SWEPT_EDGE",EDGE,{"disambiguationData":[OSD([sQuery(id+"F56.wireOp",EDGE,"E211.bottom"),sQuery(id+"F56.wireOp",EDGE,"E211.left")])]});
            var Q26;
            Q26=makeQuery(id+"F55.opExtrude","SWEPT_EDGE",EDGE,{"disambiguationData":[OSD([sQuery(id+"F54.wireOp",EDGE,"E196.top"),sQuery(id+"F54.wireOp",EDGE,"E196.right")])]});
            var Q27;
            Q27=makeQuery(id+"F57.opExtrude","SWEPT_EDGE",EDGE,{"disambiguationData":[OSD([sQuery(id+"F56.wireOp",EDGE,"E211.top"),sQuery(id+"F56.wireOp",EDGE,"E211.left")])]});
            var Q28;
            Q28=makeQuery(id+"F57.opExtrude","SWEPT_EDGE",EDGE,{"disambiguationData":[OSD([sQuery(id+"F56.wireOp",EDGE,"E214.bottom"),sQuery(id+"F56.wireOp",EDGE,"E214.right")])]});
            var Q29;
            Q29=makeQuery(id+"F55.opExtrude","SWEPT_EDGE",EDGE,{"disambiguationData":[OSD([sQuery(id+"F54.wireOp",EDGE,"E198.top"),sQuery(id+"F54.wireOp",EDGE,"E198.right")])]});
            var Q30;
            Q30=makeQuery(id+"F57.opExtrude","SWEPT_EDGE",EDGE,{"disambiguationData":[OSD([sQuery(id+"F56.wireOp",EDGE,"E214.top"),sQuery(id+"F56.wireOp",EDGE,"E214.right")])]});
            var Q31;
            Q31=makeQuery(id+"F55.opExtrude","SWEPT_EDGE",EDGE,{"disambiguationData":[OSD([sQuery(id+"F54.wireOp",EDGE,"E198.bottom"),sQuery(id+"F54.wireOp",EDGE,"E198.right")])]});
            fillet(context, id + "F58", {"entities" : qUnion([Q0, Q1, Q2, Q3, Q4, Q5, Q6, Q7, Q8, Q9, Q10, Q11, Q12, Q13, Q14, Q15, Q16, Q17, Q18, Q19, Q20, Q21, Q22, Q23, Q24, Q25, Q26, Q27, Q28, Q29, Q30, Q31]), "radius" : 0.5 * mm, "tangentPropagation" : true, "allowEdgeOverflow" : false});
        }
        {
            var Q0;
            Q0=makeQuery(id+"F8.opExtrude","CAP_FACE",FACE,{"disambiguationData":[OSD([sQuery(id+"F7.wireOp",EDGE,"E14.bottom"),sQuery(id+"F7.wireOp",EDGE,"E14.top"),sQuery(id+"F7.wireOp",EDGE,"E14.left"),sQuery(id+"F7.wireOp",EDGE,"E14.right")])],"isStart":false});
            var sketch = newSketch(context, id + "F59", { "sketchPlane" : qUnion([Q0])});
            skLineSegment(sketch, "E215.bottom", {"start": v(-87.88, 7.7) * mm, "end": v(-69.88, 7.7) * mm});
            skLineSegment(sketch, "E215.top", {"start": v(-87.88, -10.3) * mm, "end": v(-69.88, -10.3) * mm});
            skLineSegment(sketch, "E215.left", {"start": v(-87.88, 7.7) * mm, "end": v(-87.88, -10.3) * mm});
            skLineSegment(sketch, "E215.right", {"start": v(-69.88, 7.7) * mm, "end": v(-69.88, -10.3) * mm});
            skSolve(sketch);
        }
        {
            var Q0;
            Q0=qSketchRegion(id+"F59",true);
            extrude(context, id + "F60", {"entities" : qUnion([Q0]), "operationType" : NewBodyOperationType.REMOVE, "oppositeDirection" : true, "depth" : 1 * mm});
        }
        {
            var Q0;
            Q0=qCreatedBy(makeId("Top.planeOp"),FACE);
            var sketch = newSketch(context, id + "F61", { "sketchPlane" : qUnion([Q0])});
            skLineSegment(sketch, "E216.bottom", {"start": v(-55.36, 28.1) * mm, "end": v(-37.56, 28.1) * mm});
            skLineSegment(sketch, "E216.top", {"start": v(-55.36, 10.3) * mm, "end": v(-37.56, 10.3) * mm});
            skLineSegment(sketch, "E216.left", {"start": v(-55.36, 28.1) * mm, "end": v(-55.36, 10.3) * mm});
            skLineSegment(sketch, "E216.right", {"start": v(-37.56, 28.1) * mm, "end": v(-37.56, 10.3) * mm});
            skSolve(sketch);
        }
        {
            var Q0;
            Q0=qSketchRegion(id+"F61",true);
            extrude(context, id + "F62", {"entities" : qUnion([Q0]), "depth" : 1 * mm});
        }
        {
            var Q0;
            Q0=makeQuery(id+"F1.opExtrude","CAP_FACE",FACE,{"disambiguationData":[OSD([sQuery(id+"F0.wireOp",EDGE,"E1.bottom"),sQuery(id+"F0.wireOp",EDGE,"E1.top"),sQuery(id+"F0.wireOp",EDGE,"E1.left"),sQuery(id+"F0.wireOp",EDGE,"E1.right")])],"isStart":false});
            var sketch = newSketch(context, id + "F63", { "sketchPlane" : qUnion([Q0])});
            skLineSegment(sketch, "E217.bottom", {"start": v(9, 9) * mm, "end": v(-9, 9) * mm});
            skLineSegment(sketch, "E217.top", {"start": v(9, -9) * mm, "end": v(-9, -9) * mm});
            skLineSegment(sketch, "E217.left", {"start": v(9, 9) * mm, "end": v(9, -9) * mm});
            skLineSegment(sketch, "E217.right", {"start": v(-9, 9) * mm, "end": v(-9, -9) * mm});
            skPoint(sketch, "E217.middle", {"position": v(0, 0) * mm});
            skSolve(sketch);
        }
        {
            var Q0;
            Q0=qSketchRegion(id+"F63",true);
            extrude(context, id + "F64", {"entities" : qUnion([Q0]), "operationType" : NewBodyOperationType.REMOVE, "oppositeDirection" : true, "depth" : 1 * mm});
        }
    });
